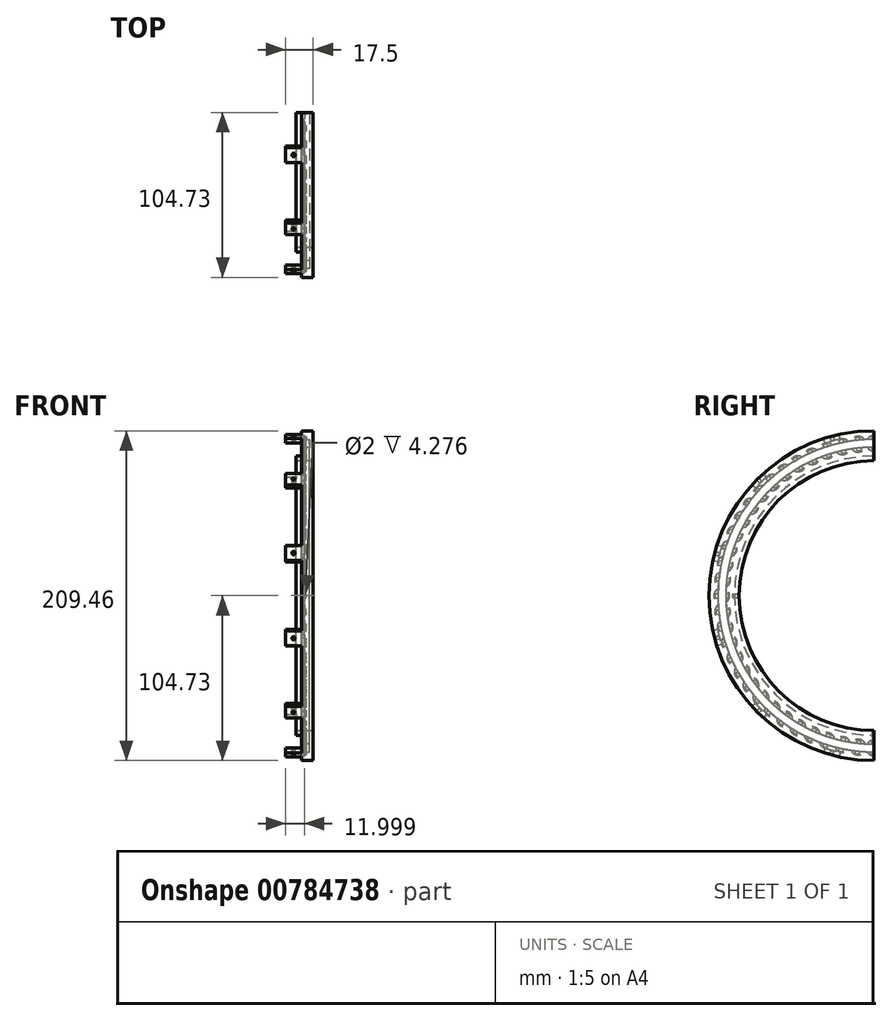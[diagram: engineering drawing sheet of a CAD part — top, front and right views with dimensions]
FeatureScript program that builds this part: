
annotation { "Feature Type Name" : "Feature", "Feature Type Description" : "" }
export const myFeature = defineFeature(function(context is Context, id is Id, definition is map)
    precondition{}
    {
        {
            var Q0;
            Q0=qCreatedBy(makeId("Front.planeOp"),FACE);
            var sketch = newSketch(context, id + "F0", { "sketchPlane" : qUnion([Q0])});
            skLineSegment(sketch, "E0.bottom", {"start": v(-125, 105) * mm, "end": v(125, 105) * mm, "construction": true});
            skLineSegment(sketch, "E0.top", {"start": v(-125, -105) * mm, "end": v(125, -105) * mm, "construction": true});
            skLineSegment(sketch, "E0.left", {"start": v(-125, 105) * mm, "end": v(-125, -105) * mm, "construction": true});
            skLineSegment(sketch, "E0.right", {"start": v(125, 105) * mm, "end": v(125, -105) * mm, "construction": true});
            skLineSegment(sketch, "E1", {"start": v(-16.75, 85.73) * mm, "end": v(-16.75, 88.73) * mm});
            skLineSegment(sketch, "E2", {"start": v(-16.75, 88.73) * mm, "end": v(-13.25, 88.73) * mm});
            skLineSegment(sketch, "E3", {"start": v(-16.75, 85.73) * mm, "end": v(-5.75, 85.73) * mm});
            skLineSegment(sketch, "E4", {"start": v(-5.75, 85.73) * mm, "end": v(-5.75, 104.73) * mm});
            skLineSegment(sketch, "E5", {"start": v(-13.25, 104.73) * mm, "end": v(-13.25, 99.23) * mm});
            skLineSegment(sketch, "E6", {"start": v(-13.25, 99.23) * mm, "end": v(-8.25, 99.23) * mm});
            skLineSegment(sketch, "E7", {"start": v(-8.25, 99.23) * mm, "end": v(-8.25, 94.23) * mm});
            skLineSegment(sketch, "E8", {"start": v(-8.25, 94.23) * mm, "end": v(-13.25, 94.23) * mm});
            skLineSegment(sketch, "E9.trimOffspring", {"start": v(-13.25, 94.23) * mm, "end": v(-13.25, 88.73) * mm});
            skLineSegment(sketch, "E10", {"start": v(-74.95, 0) * mm, "end": v(74.95, 0) * mm});
            skLineSegment(sketch, "E11", {"start": v(-13.25, 104.73) * mm, "end": v(-8.75, 104.73) * mm});
            skLineSegment(sketch, "E12.trimOffspring", {"start": v(-7.75, 104.73) * mm, "end": v(-5.75, 104.73) * mm});
            skLineSegment(sketch, "E13", {"start": v(-7.75, 104.73) * mm, "end": v(-8.75, 104.73) * mm});
            skSolve(sketch);
        }
        {
            var Q0;
            Q0=qSketchRegion(id+"F0",true);
            var Q1;
            Q1=sQuery(id+"F0.wireOp",EDGE,"E10");
            revolve(context, id + "F1", {"surfaceOperationType" : NewSurfaceOperationType.NEW, "entities" : qUnion([Q0]), "axis" : qUnion([Q1]), "revolveType" : RevolveType.ONE_DIRECTION, "angle" : 180 * degree});
        }
        {
            var Q0;
            Q0=qCreatedBy(makeId("Top.planeOp"),FACE);
            cPlane(context, id + "F2", {"entities" : qUnion([Q0]), "cplaneType" : CPlaneType.OFFSET, "offset" : 80 * mm, "oppositeDirection" : true, "width" : 150 * mm, "height" : 150 * mm});
        }
        {
            var Q0;
            Q0=qCreatedBy(id+"F2.planeOp",FACE);
            var sketch = newSketch(context, id + "F3", { "sketchPlane" : qUnion([Q0])});
            skLineSegment(sketch, "E14.top", {"start": v(-9.65, -3.1) * mm, "end": v(-12.85, -3.1) * mm, "construction": true});
            skLineSegment(sketch, "E14.left", {"start": v(-9.65, 0) * mm, "end": v(-9.65, -3.1) * mm, "construction": true});
            skLineSegment(sketch, "E14.right", {"start": v(-12.85, 0) * mm, "end": v(-12.85, -3.1) * mm, "construction": true});
            skLineSegment(sketch, "E15.top", {"start": v(-9.65, 1.57) * mm, "end": v(-12.85, 1.57) * mm, "construction": true});
            skLineSegment(sketch, "E15.left", {"start": v(-9.65, 0) * mm, "end": v(-9.65, 1.57) * mm, "construction": true});
            skLineSegment(sketch, "E15.right", {"start": v(-12.85, 0) * mm, "end": v(-12.85, 1.57) * mm, "construction": true});
            skLineSegment(sketch, "E16", {"start": v(-9.65, 0) * mm, "end": v(-12.85, 0) * mm, "construction": true});
            skLineSegment(sketch, "E17", {"start": v(-11.25, -3.1) * mm, "end": v(-11.25, 0) * mm, "construction": true});
            skCircle(sketch, "E18", {"center": v(-11.25, 0) * mm, "radius": 1 * mm});
            skSolve(sketch);
        }
        {
            var Q0;
            Q0=qSketchRegion(id+"F3",true);
            var Q1;
            Q1=makeQuery(id+"F1.opRevolve","SWEPT_FACE",FACE,{"disambiguationData":[OSD([sQuery(id+"F0.wireOp",EDGE,"E2")])]});
            extrude(context, id + "F4", {"entities" : qUnion([Q0]), "operationType" : NewBodyOperationType.REMOVE, "oppositeDirection" : true, "depth" : 10 * mm, "endBoundEntityFace" : qUnion([Q1]), "offsetDistance" : 25 * mm});
        }
        {
            var Q0;
            Q0=qCreatedBy(makeId("Front.planeOp"),FACE);
            cPlane(context, id + "F5", {"entities" : qUnion([Q0]), "cplaneType" : CPlaneType.OFFSET, "offset" : 80 * mm, "width" : 150 * mm, "height" : 150 * mm});
        }
        {
            var Q0;
            Q0=qCreatedBy(makeId("Top.planeOp"),FACE);
            cPlane(context, id + "F6", {"entities" : qUnion([Q0]), "cplaneType" : CPlaneType.OFFSET, "offset" : 80 * mm, "width" : 150 * mm, "height" : 150 * mm});
        }
        {
            var Q0;
            Q0=qCreatedBy(id+"F5.planeOp",FACE);
            var sketch = newSketch(context, id + "F7", { "sketchPlane" : qUnion([Q0])});
            skLineSegment(sketch, "E19.bottom", {"start": v(-9.65, -3.1) * mm, "end": v(-12.85, -3.1) * mm, "construction": true});
            skLineSegment(sketch, "E19.top", {"start": v(-9.65, 3.1) * mm, "end": v(-12.85, 3.1) * mm, "construction": true});
            skLineSegment(sketch, "E19.left", {"start": v(-9.65, -3.1) * mm, "end": v(-9.65, 3.1) * mm, "construction": true});
            skLineSegment(sketch, "E19.right", {"start": v(-12.85, -3.1) * mm, "end": v(-12.85, 3.1) * mm, "construction": true});
            skLineSegment(sketch, "E20", {"start": v(-11.25, 3.1) * mm, "end": v(-11.25, -3.1) * mm, "construction": true});
            skLineSegment(sketch, "E21", {"start": v(-12.85, 0) * mm, "end": v(-9.65, 0) * mm, "construction": true});
            skCircle(sketch, "E22", {"center": v(-11.25, 0) * mm, "radius": 1 * mm});
            skSolve(sketch);
        }
        {
            var Q0;
            Q0=qSketchRegion(id+"F7",true);
            var Q1;
            Q1=makeQuery(id+"F1.opRevolve","SWEPT_FACE",FACE,{"disambiguationData":[OSD([sQuery(id+"F0.wireOp",EDGE,"E2")])]});
            extrude(context, id + "F8", {"entities" : qUnion([Q0]), "operationType" : NewBodyOperationType.REMOVE, "depth" : 10 * mm, "endBoundEntityFace" : qUnion([Q1]), "offsetDistance" : 25 * mm});
        }
        {
            var Q0;
            Q0=qCreatedBy(id+"F6.planeOp",FACE);
            var sketch = newSketch(context, id + "F9", { "sketchPlane" : qUnion([Q0])});
            skLineSegment(sketch, "E23.bottom", {"start": v(-9.65, 0) * mm, "end": v(-12.85, 0) * mm, "construction": true});
            skLineSegment(sketch, "E23.top", {"start": v(-9.65, -3.1) * mm, "end": v(-12.85, -3.1) * mm, "construction": true});
            skLineSegment(sketch, "E23.left", {"start": v(-9.65, 0) * mm, "end": v(-9.65, -3.1) * mm, "construction": true});
            skLineSegment(sketch, "E23.right", {"start": v(-12.85, 0) * mm, "end": v(-12.85, -3.1) * mm, "construction": true});
            skLineSegment(sketch, "E24", {"start": v(-11.25, 0) * mm, "end": v(-11.25, -3.1) * mm, "construction": true});
            skCircle(sketch, "E25", {"center": v(-11.25, 0) * mm, "radius": 1 * mm});
            skSolve(sketch);
        }
        {
            var Q0;
            Q0=qSketchRegion(id+"F9",true);
            var Q1;
            Q1=makeQuery(id+"F1.opRevolve","SWEPT_FACE",FACE,{"disambiguationData":[OSD([sQuery(id+"F0.wireOp",EDGE,"E2")])]});
            extrude(context, id + "F10", {"entities" : qUnion([Q0]), "operationType" : NewBodyOperationType.REMOVE, "depth" : 10 * mm, "endBoundEntityFace" : qUnion([Q1]), "offsetDistance" : 25 * mm});
        }
        {
            var Q0;
            Q0=makeQuery(id+"F1.opRevolve","SWEPT_FACE",FACE,{"disambiguationData":[OSD([sQuery(id+"F0.wireOp",EDGE,"E7")])]});
            var sketch = newSketch(context, id + "F11", { "sketchPlane" : qUnion([Q0])});
            skCircle(sketch, "E26", {"center": v(0, 96.73) * mm, "radius": 5 * mm});
            skCircle(sketch, "E27.1.0", {"center": v(-10.11, 96.2) * mm, "radius": 5 * mm});
            skCircle(sketch, "E27.2.0", {"center": v(-20.11, 94.62) * mm, "radius": 5 * mm});
            skCircle(sketch, "E27.3.0", {"center": v(-29.9, 92) * mm, "radius": 5 * mm});
            skCircle(sketch, "E27.4.0", {"center": v(-39.34, 88.37) * mm, "radius": 5 * mm});
            skCircle(sketch, "E27.5.0", {"center": v(-48.36, 83.77) * mm, "radius": 5 * mm});
            skCircle(sketch, "E27.6.0", {"center": v(-56.86, 78.26) * mm, "radius": 5 * mm});
            skCircle(sketch, "E27.7.0", {"center": v(-64.73, 71.88) * mm, "radius": 5 * mm});
            skCircle(sketch, "E27.8.0", {"center": v(-71.88, 64.73) * mm, "radius": 5 * mm});
            skCircle(sketch, "E27.9.0", {"center": v(-78.26, 56.86) * mm, "radius": 5 * mm});
            skCircle(sketch, "E27.10.0", {"center": v(-83.77, 48.36) * mm, "radius": 5 * mm});
            skCircle(sketch, "E27.11.0", {"center": v(-88.37, 39.34) * mm, "radius": 5 * mm});
            skCircle(sketch, "E27.12.0", {"center": v(-92, 29.9) * mm, "radius": 5 * mm});
            skCircle(sketch, "E27.13.0", {"center": v(-94.62, 20.11) * mm, "radius": 5 * mm});
            skCircle(sketch, "E27.14.0", {"center": v(-96.2, 10.11) * mm, "radius": 5 * mm});
            skCircle(sketch, "E27.15.0", {"center": v(-96.73, 0) * mm, "radius": 5 * mm});
            skCircle(sketch, "E27.16.0", {"center": v(-96.2, -10.11) * mm, "radius": 5 * mm});
            skCircle(sketch, "E27.17.0", {"center": v(-94.62, -20.11) * mm, "radius": 5 * mm});
            skCircle(sketch, "E27.18.0", {"center": v(-92, -29.9) * mm, "radius": 5 * mm});
            skCircle(sketch, "E27.19.0", {"center": v(-88.37, -39.34) * mm, "radius": 5 * mm});
            skCircle(sketch, "E27.20.0", {"center": v(-83.77, -48.36) * mm, "radius": 5 * mm});
            skCircle(sketch, "E27.21.0", {"center": v(-78.26, -56.86) * mm, "radius": 5 * mm});
            skCircle(sketch, "E27.22.0", {"center": v(-71.88, -64.73) * mm, "radius": 5 * mm});
            skCircle(sketch, "E27.23.0", {"center": v(-64.73, -71.88) * mm, "radius": 5 * mm});
            skCircle(sketch, "E27.24.0", {"center": v(-56.86, -78.26) * mm, "radius": 5 * mm});
            skCircle(sketch, "E27.25.0", {"center": v(-48.36, -83.77) * mm, "radius": 5 * mm});
            skCircle(sketch, "E27.26.0", {"center": v(-39.34, -88.37) * mm, "radius": 5 * mm});
            skCircle(sketch, "E27.27.0", {"center": v(-29.9, -92) * mm, "radius": 5 * mm});
            skCircle(sketch, "E27.28.0", {"center": v(-20.11, -94.62) * mm, "radius": 5 * mm});
            skCircle(sketch, "E27.29.0", {"center": v(-10.11, -96.2) * mm, "radius": 5 * mm});
            skCircle(sketch, "E27.30.0", {"center": v(0, -96.73) * mm, "radius": 5 * mm});
            skCircle(sketch, "E27.31.0", {"center": v(10.11, -96.2) * mm, "radius": 5 * mm});
            skCircle(sketch, "E27.32.0", {"center": v(20.11, -94.62) * mm, "radius": 5 * mm});
            skCircle(sketch, "E27.33.0", {"center": v(29.9, -92) * mm, "radius": 5 * mm});
            skCircle(sketch, "E27.34.0", {"center": v(39.34, -88.37) * mm, "radius": 5 * mm});
            skCircle(sketch, "E27.35.0", {"center": v(48.36, -83.77) * mm, "radius": 5 * mm});
            skCircle(sketch, "E27.36.0", {"center": v(56.86, -78.26) * mm, "radius": 5 * mm});
            skCircle(sketch, "E27.37.0", {"center": v(64.73, -71.88) * mm, "radius": 5 * mm});
            skCircle(sketch, "E27.38.0", {"center": v(71.88, -64.73) * mm, "radius": 5 * mm});
            skCircle(sketch, "E27.39.0", {"center": v(78.26, -56.86) * mm, "radius": 5 * mm});
            skCircle(sketch, "E27.40.0", {"center": v(83.77, -48.37) * mm, "radius": 5 * mm});
            skCircle(sketch, "E27.41.0", {"center": v(88.37, -39.34) * mm, "radius": 5 * mm});
            skCircle(sketch, "E27.42.0", {"center": v(92, -29.9) * mm, "radius": 5 * mm});
            skCircle(sketch, "E27.43.0", {"center": v(94.62, -20.11) * mm, "radius": 5 * mm});
            skCircle(sketch, "E27.44.0", {"center": v(96.2, -10.11) * mm, "radius": 5 * mm});
            skCircle(sketch, "E27.45.0", {"center": v(96.73, 0) * mm, "radius": 5 * mm});
            skCircle(sketch, "E27.46.0", {"center": v(96.2, 10.11) * mm, "radius": 5 * mm});
            skCircle(sketch, "E27.47.0", {"center": v(94.62, 20.11) * mm, "radius": 5 * mm});
            skCircle(sketch, "E27.48.0", {"center": v(92, 29.9) * mm, "radius": 5 * mm});
            skCircle(sketch, "E27.49.0", {"center": v(88.37, 39.34) * mm, "radius": 5 * mm});
            skCircle(sketch, "E27.50.0", {"center": v(83.77, 48.36) * mm, "radius": 5 * mm});
            skCircle(sketch, "E27.51.0", {"center": v(78.26, 56.86) * mm, "radius": 5 * mm});
            skCircle(sketch, "E27.52.0", {"center": v(71.88, 64.73) * mm, "radius": 5 * mm});
            skCircle(sketch, "E27.53.0", {"center": v(64.73, 71.88) * mm, "radius": 5 * mm});
            skCircle(sketch, "E27.54.0", {"center": v(56.86, 78.26) * mm, "radius": 5 * mm});
            skCircle(sketch, "E27.55.0", {"center": v(48.36, 83.77) * mm, "radius": 5 * mm});
            skCircle(sketch, "E27.56.0", {"center": v(39.34, 88.37) * mm, "radius": 5 * mm});
            skCircle(sketch, "E27.57.0", {"center": v(29.9, 92) * mm, "radius": 5 * mm});
            skCircle(sketch, "E27.58.0", {"center": v(20.11, 94.62) * mm, "radius": 5 * mm});
            skCircle(sketch, "E27.59.0", {"center": v(10.11, 96.2) * mm, "radius": 5 * mm});
            skPoint(sketch, "E27.center", {"position": v(0, 0) * mm});
            skSolve(sketch);
        }
        {
            var Q0;
            Q0=qSketchRegion(id+"F11",true);
            extrude(context, id + "F12", {"entities" : qUnion([Q0]), "operationType" : NewBodyOperationType.REMOVE, "depth" : 25 * mm, "offsetDistance" : 25 * mm, "hasSecondDirection" : true, "secondDirectionOppositeDirection" : false, "secondDirectionDepth" : 3 * mm});
        }
        {
            var Q0;
            Q0=makeQuery(id+"F1.opRevolve","SWEPT_FACE",FACE,{"disambiguationData":[OSD([sQuery(id+"F0.wireOp",EDGE,"E7")])]});
            var sketch = newSketch(context, id + "F13", { "sketchPlane" : qUnion([Q0])});
            skLineSegment(sketch, "E28.bottom", {"start": v(1.36, 92.48) * mm, "end": v(0, 92.48) * mm});
            skLineSegment(sketch, "E28.top", {"start": v(1.36, 100.98) * mm, "end": v(0, 100.98) * mm});
            skLineSegment(sketch, "E28.left", {"start": v(1.36, 92.48) * mm, "end": v(1.36, 100.98) * mm});
            skLineSegment(sketch, "E29", {"start": v(1.96, 96.73) * mm, "end": v(-1.46, 96.73) * mm, "construction": true});
            skLineSegment(sketch, "E30.MirrorCS", {"start": v(-1.36, 92.48) * mm, "end": v(0, 92.48) * mm});
            skLineSegment(sketch, "E31.MirrorCS", {"start": v(-1.36, 92.48) * mm, "end": v(-1.36, 100.98) * mm});
            skLineSegment(sketch, "E32.MirrorCS", {"start": v(-1.36, 100.98) * mm, "end": v(0, 100.98) * mm});
            skLineSegment(sketch, "E33", {"start": v(0, 92.48) * mm, "end": v(0, 100.98) * mm, "construction": true});
            skLineSegment(sketch, "E34.1.0", {"start": v(-8.32, 92.12) * mm, "end": v(-9.67, 91.97) * mm});
            skLineSegment(sketch, "E34.1.1", {"start": v(-9.2, 100.57) * mm, "end": v(-10.56, 100.43) * mm});
            skLineSegment(sketch, "E34.1.2", {"start": v(-8.32, 92.12) * mm, "end": v(-9.2, 100.57) * mm});
            skLineSegment(sketch, "E34.1.3", {"start": v(-8.16, 96.4) * mm, "end": v(-11.56, 96.05) * mm, "construction": true});
            skLineSegment(sketch, "E34.1.4", {"start": v(-11.02, 91.83) * mm, "end": v(-9.67, 91.97) * mm});
            skLineSegment(sketch, "E34.1.5", {"start": v(-11.02, 91.83) * mm, "end": v(-11.9, 100.28) * mm});
            skLineSegment(sketch, "E34.1.6", {"start": v(-11.9, 100.28) * mm, "end": v(-10.56, 100.43) * mm});
            skLineSegment(sketch, "E34.1.7", {"start": v(-9.67, 91.97) * mm, "end": v(-10.56, 100.43) * mm, "construction": true});
            skLineSegment(sketch, "E34.2.0", {"start": v(-17.9, 90.74) * mm, "end": v(-19.23, 90.46) * mm});
            skLineSegment(sketch, "E34.2.1", {"start": v(-19.67, 99.06) * mm, "end": v(-21, 98.77) * mm});
            skLineSegment(sketch, "E34.2.2", {"start": v(-17.9, 90.74) * mm, "end": v(-19.67, 99.06) * mm});
            skLineSegment(sketch, "E34.2.3", {"start": v(-18.2, 95.02) * mm, "end": v(-21.54, 94.31) * mm, "construction": true});
            skLineSegment(sketch, "E34.2.4", {"start": v(-20.56, 90.18) * mm, "end": v(-19.23, 90.46) * mm});
            skLineSegment(sketch, "E34.2.5", {"start": v(-20.56, 90.18) * mm, "end": v(-22.32, 98.5) * mm});
            skLineSegment(sketch, "E34.2.6", {"start": v(-22.32, 98.5) * mm, "end": v(-21, 98.77) * mm});
            skLineSegment(sketch, "E34.2.7", {"start": v(-19.23, 90.46) * mm, "end": v(-21, 98.77) * mm, "construction": true});
            skLineSegment(sketch, "E34.3.0", {"start": v(-27.29, 88.37) * mm, "end": v(-28.58, 87.95) * mm});
            skLineSegment(sketch, "E34.3.1", {"start": v(-29.91, 96.46) * mm, "end": v(-31.2, 96.04) * mm});
            skLineSegment(sketch, "E34.3.2", {"start": v(-27.29, 88.37) * mm, "end": v(-29.91, 96.46) * mm});
            skLineSegment(sketch, "E34.3.3", {"start": v(-28.02, 92.6) * mm, "end": v(-31.28, 91.54) * mm, "construction": true});
            skLineSegment(sketch, "E34.3.4", {"start": v(-29.87, 87.53) * mm, "end": v(-28.58, 87.95) * mm});
            skLineSegment(sketch, "E34.3.5", {"start": v(-29.87, 87.53) * mm, "end": v(-32.5, 95.62) * mm});
            skLineSegment(sketch, "E34.3.6", {"start": v(-32.5, 95.62) * mm, "end": v(-31.2, 96.04) * mm});
            skLineSegment(sketch, "E34.3.7", {"start": v(-28.58, 87.95) * mm, "end": v(-31.2, 96.04) * mm, "construction": true});
            skLineSegment(sketch, "E34.4.0", {"start": v(-36.37, 85.04) * mm, "end": v(-37.62, 84.48) * mm});
            skLineSegment(sketch, "E34.4.1", {"start": v(-39.83, 92.8) * mm, "end": v(-41.07, 92.25) * mm});
            skLineSegment(sketch, "E34.4.2", {"start": v(-36.37, 85.04) * mm, "end": v(-39.83, 92.8) * mm});
            skLineSegment(sketch, "E34.4.3", {"start": v(-37.55, 89.17) * mm, "end": v(-40.68, 87.77) * mm, "construction": true});
            skLineSegment(sketch, "E34.4.4", {"start": v(-38.86, 83.93) * mm, "end": v(-37.62, 84.48) * mm});
            skLineSegment(sketch, "E34.4.5", {"start": v(-38.86, 83.93) * mm, "end": v(-42.31, 91.7) * mm});
            skLineSegment(sketch, "E34.4.6", {"start": v(-42.31, 91.7) * mm, "end": v(-41.07, 92.25) * mm});
            skLineSegment(sketch, "E34.4.7", {"start": v(-37.62, 84.48) * mm, "end": v(-41.07, 92.25) * mm, "construction": true});
            skLineSegment(sketch, "E34.5.0", {"start": v(-45.06, 80.77) * mm, "end": v(-46.24, 80.1) * mm});
            skLineSegment(sketch, "E34.5.1", {"start": v(-49.31, 88.13) * mm, "end": v(-50.49, 87.45) * mm});
            skLineSegment(sketch, "E34.5.2", {"start": v(-45.06, 80.77) * mm, "end": v(-49.31, 88.13) * mm});
            skLineSegment(sketch, "E34.5.3", {"start": v(-46.67, 84.75) * mm, "end": v(-49.63, 83.04) * mm, "construction": true});
            skLineSegment(sketch, "E34.5.4", {"start": v(-47.42, 79.41) * mm, "end": v(-46.24, 80.1) * mm});
            skLineSegment(sketch, "E34.5.5", {"start": v(-47.42, 79.41) * mm, "end": v(-51.67, 86.77) * mm});
            skLineSegment(sketch, "E34.5.6", {"start": v(-51.67, 86.77) * mm, "end": v(-50.49, 87.45) * mm});
            skLineSegment(sketch, "E34.5.7", {"start": v(-46.24, 80.1) * mm, "end": v(-50.49, 87.45) * mm, "construction": true});
            skLineSegment(sketch, "E34.6.0", {"start": v(-53.26, 75.62) * mm, "end": v(-54.36, 74.82) * mm});
            skLineSegment(sketch, "E34.6.1", {"start": v(-58.26, 82.5) * mm, "end": v(-59.35, 81.7) * mm});
            skLineSegment(sketch, "E34.6.2", {"start": v(-53.26, 75.62) * mm, "end": v(-58.26, 82.5) * mm});
            skLineSegment(sketch, "E34.6.3", {"start": v(-55.27, 79.4) * mm, "end": v(-58.04, 77.4) * mm, "construction": true});
            skLineSegment(sketch, "E34.6.4", {"start": v(-55.46, 74.02) * mm, "end": v(-54.36, 74.82) * mm});
            skLineSegment(sketch, "E34.6.5", {"start": v(-55.46, 74.02) * mm, "end": v(-60.45, 80.9) * mm});
            skLineSegment(sketch, "E34.6.6", {"start": v(-60.45, 80.9) * mm, "end": v(-59.35, 81.7) * mm});
            skLineSegment(sketch, "E34.6.7", {"start": v(-54.36, 74.82) * mm, "end": v(-59.35, 81.7) * mm, "construction": true});
            skLineSegment(sketch, "E34.7.0", {"start": v(-60.87, 69.63) * mm, "end": v(-61.88, 68.73) * mm});
            skLineSegment(sketch, "E34.7.1", {"start": v(-66.56, 75.95) * mm, "end": v(-67.57, 75.04) * mm});
            skLineSegment(sketch, "E34.7.2", {"start": v(-60.87, 69.63) * mm, "end": v(-66.56, 75.95) * mm});
            skLineSegment(sketch, "E34.7.3", {"start": v(-63.27, 73.2) * mm, "end": v(-65.8, 70.9) * mm, "construction": true});
            skLineSegment(sketch, "E34.7.4", {"start": v(-62.9, 67.82) * mm, "end": v(-61.88, 68.73) * mm});
            skLineSegment(sketch, "E34.7.5", {"start": v(-62.9, 67.82) * mm, "end": v(-68.58, 74.13) * mm});
            skLineSegment(sketch, "E34.7.6", {"start": v(-68.58, 74.13) * mm, "end": v(-67.57, 75.04) * mm});
            skLineSegment(sketch, "E34.7.7", {"start": v(-61.88, 68.73) * mm, "end": v(-67.57, 75.04) * mm, "construction": true});
            skLineSegment(sketch, "E34.8.0", {"start": v(-67.82, 62.9) * mm, "end": v(-68.73, 61.88) * mm});
            skLineSegment(sketch, "E34.8.1", {"start": v(-74.13, 68.58) * mm, "end": v(-75.04, 67.57) * mm});
            skLineSegment(sketch, "E34.8.2", {"start": v(-67.82, 62.9) * mm, "end": v(-74.13, 68.58) * mm});
            skLineSegment(sketch, "E34.8.3", {"start": v(-70.57, 66.18) * mm, "end": v(-72.86, 63.64) * mm, "construction": true});
            skLineSegment(sketch, "E34.8.4", {"start": v(-69.63, 60.87) * mm, "end": v(-68.73, 61.88) * mm});
            skLineSegment(sketch, "E34.8.5", {"start": v(-69.63, 60.87) * mm, "end": v(-75.95, 66.56) * mm});
            skLineSegment(sketch, "E34.8.6", {"start": v(-75.95, 66.56) * mm, "end": v(-75.04, 67.57) * mm});
            skLineSegment(sketch, "E34.8.7", {"start": v(-68.73, 61.88) * mm, "end": v(-75.04, 67.57) * mm, "construction": true});
            skLineSegment(sketch, "E34.9.0", {"start": v(-74.02, 55.46) * mm, "end": v(-74.82, 54.36) * mm});
            skLineSegment(sketch, "E34.9.1", {"start": v(-80.9, 60.45) * mm, "end": v(-81.7, 59.35) * mm});
            skLineSegment(sketch, "E34.9.2", {"start": v(-74.02, 55.46) * mm, "end": v(-80.9, 60.45) * mm});
            skLineSegment(sketch, "E34.9.3", {"start": v(-77.1, 58.44) * mm, "end": v(-79.11, 55.68) * mm, "construction": true});
            skLineSegment(sketch, "E34.9.4", {"start": v(-75.62, 53.26) * mm, "end": v(-74.82, 54.36) * mm});
            skLineSegment(sketch, "E34.9.5", {"start": v(-75.62, 53.26) * mm, "end": v(-82.5, 58.26) * mm});
            skLineSegment(sketch, "E34.9.6", {"start": v(-82.5, 58.26) * mm, "end": v(-81.7, 59.35) * mm});
            skLineSegment(sketch, "E34.9.7", {"start": v(-74.82, 54.36) * mm, "end": v(-81.7, 59.35) * mm, "construction": true});
            skLineSegment(sketch, "E34.10.0", {"start": v(-79.41, 47.42) * mm, "end": v(-80.1, 46.24) * mm});
            skLineSegment(sketch, "E34.10.1", {"start": v(-86.77, 51.67) * mm, "end": v(-87.45, 50.49) * mm});
            skLineSegment(sketch, "E34.10.2", {"start": v(-79.41, 47.42) * mm, "end": v(-86.77, 51.67) * mm});
            skLineSegment(sketch, "E34.10.3", {"start": v(-82.79, 50.06) * mm, "end": v(-84.5, 47.1) * mm, "construction": true});
            skLineSegment(sketch, "E34.10.4", {"start": v(-80.77, 45.06) * mm, "end": v(-80.1, 46.24) * mm});
            skLineSegment(sketch, "E34.10.5", {"start": v(-80.77, 45.06) * mm, "end": v(-88.13, 49.31) * mm});
            skLineSegment(sketch, "E34.10.6", {"start": v(-88.13, 49.31) * mm, "end": v(-87.45, 50.49) * mm});
            skLineSegment(sketch, "E34.10.7", {"start": v(-80.1, 46.24) * mm, "end": v(-87.45, 50.49) * mm, "construction": true});
            skLineSegment(sketch, "E34.11.0", {"start": v(-83.93, 38.86) * mm, "end": v(-84.48, 37.62) * mm});
            skLineSegment(sketch, "E34.11.1", {"start": v(-91.7, 42.31) * mm, "end": v(-92.25, 41.07) * mm});
            skLineSegment(sketch, "E34.11.2", {"start": v(-83.93, 38.86) * mm, "end": v(-91.7, 42.31) * mm});
            skLineSegment(sketch, "E34.11.3", {"start": v(-87.57, 41.14) * mm, "end": v(-88.96, 38) * mm, "construction": true});
            skLineSegment(sketch, "E34.11.4", {"start": v(-85.04, 36.37) * mm, "end": v(-84.48, 37.62) * mm});
            skLineSegment(sketch, "E34.11.5", {"start": v(-85.04, 36.37) * mm, "end": v(-92.8, 39.83) * mm});
            skLineSegment(sketch, "E34.11.6", {"start": v(-92.8, 39.83) * mm, "end": v(-92.25, 41.07) * mm});
            skLineSegment(sketch, "E34.11.7", {"start": v(-84.48, 37.62) * mm, "end": v(-92.25, 41.07) * mm, "construction": true});
            skLineSegment(sketch, "E34.12.0", {"start": v(-87.53, 29.87) * mm, "end": v(-87.95, 28.58) * mm});
            skLineSegment(sketch, "E34.12.1", {"start": v(-95.62, 32.5) * mm, "end": v(-96.04, 31.2) * mm});
            skLineSegment(sketch, "E34.12.2", {"start": v(-87.53, 29.87) * mm, "end": v(-95.62, 32.5) * mm});
            skLineSegment(sketch, "E34.12.3", {"start": v(-91.39, 31.76) * mm, "end": v(-92.45, 28.5) * mm, "construction": true});
            skLineSegment(sketch, "E34.12.4", {"start": v(-88.37, 27.29) * mm, "end": v(-87.95, 28.58) * mm});
            skLineSegment(sketch, "E34.12.5", {"start": v(-88.37, 27.29) * mm, "end": v(-96.46, 29.91) * mm});
            skLineSegment(sketch, "E34.12.6", {"start": v(-96.46, 29.91) * mm, "end": v(-96.04, 31.2) * mm});
            skLineSegment(sketch, "E34.12.7", {"start": v(-87.95, 28.58) * mm, "end": v(-96.04, 31.2) * mm, "construction": true});
            skLineSegment(sketch, "E34.13.0", {"start": v(-90.18, 20.56) * mm, "end": v(-90.46, 19.23) * mm});
            skLineSegment(sketch, "E34.13.1", {"start": v(-98.5, 22.32) * mm, "end": v(-98.77, 21) * mm});
            skLineSegment(sketch, "E34.13.2", {"start": v(-90.18, 20.56) * mm, "end": v(-98.5, 22.32) * mm});
            skLineSegment(sketch, "E34.13.3", {"start": v(-94.2, 22.03) * mm, "end": v(-94.92, 18.68) * mm, "construction": true});
            skLineSegment(sketch, "E34.13.4", {"start": v(-90.74, 17.9) * mm, "end": v(-90.46, 19.23) * mm});
            skLineSegment(sketch, "E34.13.5", {"start": v(-90.74, 17.9) * mm, "end": v(-99.06, 19.67) * mm});
            skLineSegment(sketch, "E34.13.6", {"start": v(-99.06, 19.67) * mm, "end": v(-98.77, 21) * mm});
            skLineSegment(sketch, "E34.13.7", {"start": v(-90.46, 19.23) * mm, "end": v(-98.77, 21) * mm, "construction": true});
            skLineSegment(sketch, "E34.14.0", {"start": v(-91.83, 11.02) * mm, "end": v(-91.97, 9.67) * mm});
            skLineSegment(sketch, "E34.14.1", {"start": v(-100.28, 11.9) * mm, "end": v(-100.43, 10.56) * mm});
            skLineSegment(sketch, "E34.14.2", {"start": v(-91.83, 11.02) * mm, "end": v(-100.28, 11.9) * mm});
            skLineSegment(sketch, "E34.14.3", {"start": v(-96, 12.06) * mm, "end": v(-96.35, 8.66) * mm, "construction": true});
            skLineSegment(sketch, "E34.14.4", {"start": v(-92.12, 8.32) * mm, "end": v(-91.97, 9.67) * mm});
            skLineSegment(sketch, "E34.14.5", {"start": v(-92.12, 8.32) * mm, "end": v(-100.57, 9.2) * mm});
            skLineSegment(sketch, "E34.14.6", {"start": v(-100.57, 9.2) * mm, "end": v(-100.43, 10.56) * mm});
            skLineSegment(sketch, "E34.14.7", {"start": v(-91.97, 9.67) * mm, "end": v(-100.43, 10.56) * mm, "construction": true});
            skLineSegment(sketch, "E34.15.0", {"start": v(-92.48, 1.36) * mm, "end": v(-92.48, 0) * mm});
            skLineSegment(sketch, "E34.15.1", {"start": v(-100.98, 1.36) * mm, "end": v(-100.98, 0) * mm});
            skLineSegment(sketch, "E34.15.2", {"start": v(-92.48, 1.36) * mm, "end": v(-100.98, 1.36) * mm});
            skLineSegment(sketch, "E34.15.3", {"start": v(-96.73, 1.96) * mm, "end": v(-96.73, -1.46) * mm, "construction": true});
            skLineSegment(sketch, "E34.15.4", {"start": v(-92.48, -1.36) * mm, "end": v(-92.48, 0) * mm});
            skLineSegment(sketch, "E34.15.5", {"start": v(-92.48, -1.36) * mm, "end": v(-100.98, -1.36) * mm});
            skLineSegment(sketch, "E34.15.6", {"start": v(-100.98, -1.36) * mm, "end": v(-100.98, 0) * mm});
            skLineSegment(sketch, "E34.15.7", {"start": v(-92.48, 0) * mm, "end": v(-100.98, 0) * mm, "construction": true});
            skLineSegment(sketch, "E34.16.0", {"start": v(-92.12, -8.32) * mm, "end": v(-91.97, -9.67) * mm});
            skLineSegment(sketch, "E34.16.1", {"start": v(-100.57, -9.2) * mm, "end": v(-100.43, -10.56) * mm});
            skLineSegment(sketch, "E34.16.2", {"start": v(-92.12, -8.32) * mm, "end": v(-100.57, -9.2) * mm});
            skLineSegment(sketch, "E34.16.3", {"start": v(-96.4, -8.16) * mm, "end": v(-96.05, -11.56) * mm, "construction": true});
            skLineSegment(sketch, "E34.16.4", {"start": v(-91.83, -11.02) * mm, "end": v(-91.97, -9.67) * mm});
            skLineSegment(sketch, "E34.16.5", {"start": v(-91.83, -11.02) * mm, "end": v(-100.28, -11.9) * mm});
            skLineSegment(sketch, "E34.16.6", {"start": v(-100.28, -11.9) * mm, "end": v(-100.43, -10.56) * mm});
            skLineSegment(sketch, "E34.16.7", {"start": v(-91.97, -9.67) * mm, "end": v(-100.43, -10.56) * mm, "construction": true});
            skLineSegment(sketch, "E34.17.0", {"start": v(-90.74, -17.9) * mm, "end": v(-90.46, -19.23) * mm});
            skLineSegment(sketch, "E34.17.1", {"start": v(-99.06, -19.67) * mm, "end": v(-98.77, -21) * mm});
            skLineSegment(sketch, "E34.17.2", {"start": v(-90.74, -17.9) * mm, "end": v(-99.06, -19.67) * mm});
            skLineSegment(sketch, "E34.17.3", {"start": v(-95.02, -18.2) * mm, "end": v(-94.31, -21.54) * mm, "construction": true});
            skLineSegment(sketch, "E34.17.4", {"start": v(-90.18, -20.56) * mm, "end": v(-90.46, -19.23) * mm});
            skLineSegment(sketch, "E34.17.5", {"start": v(-90.18, -20.56) * mm, "end": v(-98.5, -22.32) * mm});
            skLineSegment(sketch, "E34.17.6", {"start": v(-98.5, -22.32) * mm, "end": v(-98.77, -21) * mm});
            skLineSegment(sketch, "E34.17.7", {"start": v(-90.46, -19.23) * mm, "end": v(-98.77, -21) * mm, "construction": true});
            skLineSegment(sketch, "E34.18.0", {"start": v(-88.37, -27.29) * mm, "end": v(-87.95, -28.58) * mm});
            skLineSegment(sketch, "E34.18.1", {"start": v(-96.46, -29.91) * mm, "end": v(-96.04, -31.2) * mm});
            skLineSegment(sketch, "E34.18.2", {"start": v(-88.37, -27.29) * mm, "end": v(-96.46, -29.91) * mm});
            skLineSegment(sketch, "E34.18.3", {"start": v(-92.6, -28.02) * mm, "end": v(-91.54, -31.28) * mm, "construction": true});
            skLineSegment(sketch, "E34.18.4", {"start": v(-87.53, -29.87) * mm, "end": v(-87.95, -28.58) * mm});
            skLineSegment(sketch, "E34.18.5", {"start": v(-87.53, -29.87) * mm, "end": v(-95.62, -32.5) * mm});
            skLineSegment(sketch, "E34.18.6", {"start": v(-95.62, -32.5) * mm, "end": v(-96.04, -31.2) * mm});
            skLineSegment(sketch, "E34.18.7", {"start": v(-87.95, -28.58) * mm, "end": v(-96.04, -31.2) * mm, "construction": true});
            skLineSegment(sketch, "E34.19.0", {"start": v(-85.04, -36.37) * mm, "end": v(-84.48, -37.62) * mm});
            skLineSegment(sketch, "E34.19.1", {"start": v(-92.8, -39.83) * mm, "end": v(-92.25, -41.07) * mm});
            skLineSegment(sketch, "E34.19.2", {"start": v(-85.04, -36.37) * mm, "end": v(-92.8, -39.83) * mm});
            skLineSegment(sketch, "E34.19.3", {"start": v(-89.17, -37.55) * mm, "end": v(-87.77, -40.68) * mm, "construction": true});
            skLineSegment(sketch, "E34.19.4", {"start": v(-83.93, -38.86) * mm, "end": v(-84.48, -37.62) * mm});
            skLineSegment(sketch, "E34.19.5", {"start": v(-83.93, -38.86) * mm, "end": v(-91.7, -42.31) * mm});
            skLineSegment(sketch, "E34.19.6", {"start": v(-91.7, -42.31) * mm, "end": v(-92.25, -41.07) * mm});
            skLineSegment(sketch, "E34.19.7", {"start": v(-84.48, -37.62) * mm, "end": v(-92.25, -41.07) * mm, "construction": true});
            skLineSegment(sketch, "E34.20.0", {"start": v(-80.77, -45.06) * mm, "end": v(-80.1, -46.24) * mm});
            skLineSegment(sketch, "E34.20.1", {"start": v(-88.13, -49.31) * mm, "end": v(-87.45, -50.49) * mm});
            skLineSegment(sketch, "E34.20.2", {"start": v(-80.77, -45.06) * mm, "end": v(-88.13, -49.31) * mm});
            skLineSegment(sketch, "E34.20.3", {"start": v(-84.75, -46.67) * mm, "end": v(-83.04, -49.63) * mm, "construction": true});
            skLineSegment(sketch, "E34.20.4", {"start": v(-79.41, -47.42) * mm, "end": v(-80.1, -46.24) * mm});
            skLineSegment(sketch, "E34.20.5", {"start": v(-79.41, -47.42) * mm, "end": v(-86.77, -51.67) * mm});
            skLineSegment(sketch, "E34.20.6", {"start": v(-86.77, -51.67) * mm, "end": v(-87.45, -50.49) * mm});
            skLineSegment(sketch, "E34.20.7", {"start": v(-80.1, -46.24) * mm, "end": v(-87.45, -50.49) * mm, "construction": true});
            skLineSegment(sketch, "E34.21.0", {"start": v(-75.62, -53.26) * mm, "end": v(-74.82, -54.36) * mm});
            skLineSegment(sketch, "E34.21.1", {"start": v(-82.5, -58.26) * mm, "end": v(-81.7, -59.35) * mm});
            skLineSegment(sketch, "E34.21.2", {"start": v(-75.62, -53.26) * mm, "end": v(-82.5, -58.26) * mm});
            skLineSegment(sketch, "E34.21.3", {"start": v(-79.4, -55.27) * mm, "end": v(-77.4, -58.04) * mm, "construction": true});
            skLineSegment(sketch, "E34.21.4", {"start": v(-74.02, -55.46) * mm, "end": v(-74.82, -54.36) * mm});
            skLineSegment(sketch, "E34.21.5", {"start": v(-74.02, -55.46) * mm, "end": v(-80.9, -60.45) * mm});
            skLineSegment(sketch, "E34.21.6", {"start": v(-80.9, -60.45) * mm, "end": v(-81.7, -59.35) * mm});
            skLineSegment(sketch, "E34.21.7", {"start": v(-74.82, -54.36) * mm, "end": v(-81.7, -59.35) * mm, "construction": true});
            skLineSegment(sketch, "E34.22.0", {"start": v(-69.63, -60.87) * mm, "end": v(-68.73, -61.88) * mm});
            skLineSegment(sketch, "E34.22.1", {"start": v(-75.95, -66.56) * mm, "end": v(-75.04, -67.57) * mm});
            skLineSegment(sketch, "E34.22.2", {"start": v(-69.63, -60.87) * mm, "end": v(-75.95, -66.56) * mm});
            skLineSegment(sketch, "E34.22.3", {"start": v(-73.2, -63.27) * mm, "end": v(-70.9, -65.8) * mm, "construction": true});
            skLineSegment(sketch, "E34.22.4", {"start": v(-67.82, -62.9) * mm, "end": v(-68.73, -61.88) * mm});
            skLineSegment(sketch, "E34.22.5", {"start": v(-67.82, -62.9) * mm, "end": v(-74.13, -68.58) * mm});
            skLineSegment(sketch, "E34.22.6", {"start": v(-74.13, -68.58) * mm, "end": v(-75.04, -67.57) * mm});
            skLineSegment(sketch, "E34.22.7", {"start": v(-68.73, -61.88) * mm, "end": v(-75.04, -67.57) * mm, "construction": true});
            skLineSegment(sketch, "E34.23.0", {"start": v(-62.9, -67.82) * mm, "end": v(-61.88, -68.73) * mm});
            skLineSegment(sketch, "E34.23.1", {"start": v(-68.58, -74.13) * mm, "end": v(-67.57, -75.04) * mm});
            skLineSegment(sketch, "E34.23.2", {"start": v(-62.9, -67.82) * mm, "end": v(-68.58, -74.13) * mm});
            skLineSegment(sketch, "E34.23.3", {"start": v(-66.18, -70.57) * mm, "end": v(-63.64, -72.86) * mm, "construction": true});
            skLineSegment(sketch, "E34.23.4", {"start": v(-60.87, -69.63) * mm, "end": v(-61.88, -68.73) * mm});
            skLineSegment(sketch, "E34.23.5", {"start": v(-60.87, -69.63) * mm, "end": v(-66.56, -75.95) * mm});
            skLineSegment(sketch, "E34.23.6", {"start": v(-66.56, -75.95) * mm, "end": v(-67.57, -75.04) * mm});
            skLineSegment(sketch, "E34.23.7", {"start": v(-61.88, -68.73) * mm, "end": v(-67.57, -75.04) * mm, "construction": true});
            skLineSegment(sketch, "E34.24.0", {"start": v(-55.46, -74.02) * mm, "end": v(-54.36, -74.82) * mm});
            skLineSegment(sketch, "E34.24.1", {"start": v(-60.45, -80.9) * mm, "end": v(-59.35, -81.7) * mm});
            skLineSegment(sketch, "E34.24.2", {"start": v(-55.46, -74.02) * mm, "end": v(-60.45, -80.9) * mm});
            skLineSegment(sketch, "E34.24.3", {"start": v(-58.44, -77.1) * mm, "end": v(-55.68, -79.11) * mm, "construction": true});
            skLineSegment(sketch, "E34.24.4", {"start": v(-53.26, -75.62) * mm, "end": v(-54.36, -74.82) * mm});
            skLineSegment(sketch, "E34.24.5", {"start": v(-53.26, -75.62) * mm, "end": v(-58.26, -82.5) * mm});
            skLineSegment(sketch, "E34.24.6", {"start": v(-58.26, -82.5) * mm, "end": v(-59.35, -81.7) * mm});
            skLineSegment(sketch, "E34.24.7", {"start": v(-54.36, -74.82) * mm, "end": v(-59.35, -81.7) * mm, "construction": true});
            skLineSegment(sketch, "E34.25.0", {"start": v(-47.42, -79.41) * mm, "end": v(-46.24, -80.1) * mm});
            skLineSegment(sketch, "E34.25.1", {"start": v(-51.67, -86.77) * mm, "end": v(-50.49, -87.45) * mm});
            skLineSegment(sketch, "E34.25.2", {"start": v(-47.42, -79.41) * mm, "end": v(-51.67, -86.77) * mm});
            skLineSegment(sketch, "E34.25.3", {"start": v(-50.06, -82.79) * mm, "end": v(-47.1, -84.5) * mm, "construction": true});
            skLineSegment(sketch, "E34.25.4", {"start": v(-45.06, -80.77) * mm, "end": v(-46.24, -80.1) * mm});
            skLineSegment(sketch, "E34.25.5", {"start": v(-45.06, -80.77) * mm, "end": v(-49.31, -88.13) * mm});
            skLineSegment(sketch, "E34.25.6", {"start": v(-49.31, -88.13) * mm, "end": v(-50.49, -87.45) * mm});
            skLineSegment(sketch, "E34.25.7", {"start": v(-46.24, -80.1) * mm, "end": v(-50.49, -87.45) * mm, "construction": true});
            skLineSegment(sketch, "E34.26.0", {"start": v(-38.86, -83.93) * mm, "end": v(-37.62, -84.48) * mm});
            skLineSegment(sketch, "E34.26.1", {"start": v(-42.31, -91.7) * mm, "end": v(-41.07, -92.25) * mm});
            skLineSegment(sketch, "E34.26.2", {"start": v(-38.86, -83.93) * mm, "end": v(-42.31, -91.7) * mm});
            skLineSegment(sketch, "E34.26.3", {"start": v(-41.14, -87.57) * mm, "end": v(-38, -88.96) * mm, "construction": true});
            skLineSegment(sketch, "E34.26.4", {"start": v(-36.37, -85.04) * mm, "end": v(-37.62, -84.48) * mm});
            skLineSegment(sketch, "E34.26.5", {"start": v(-36.37, -85.04) * mm, "end": v(-39.83, -92.8) * mm});
            skLineSegment(sketch, "E34.26.6", {"start": v(-39.83, -92.8) * mm, "end": v(-41.07, -92.25) * mm});
            skLineSegment(sketch, "E34.26.7", {"start": v(-37.62, -84.48) * mm, "end": v(-41.07, -92.25) * mm, "construction": true});
            skLineSegment(sketch, "E34.27.0", {"start": v(-29.87, -87.53) * mm, "end": v(-28.58, -87.95) * mm});
            skLineSegment(sketch, "E34.27.1", {"start": v(-32.5, -95.62) * mm, "end": v(-31.2, -96.04) * mm});
            skLineSegment(sketch, "E34.27.2", {"start": v(-29.87, -87.53) * mm, "end": v(-32.5, -95.62) * mm});
            skLineSegment(sketch, "E34.27.3", {"start": v(-31.76, -91.39) * mm, "end": v(-28.5, -92.45) * mm, "construction": true});
            skLineSegment(sketch, "E34.27.4", {"start": v(-27.29, -88.37) * mm, "end": v(-28.58, -87.95) * mm});
            skLineSegment(sketch, "E34.27.5", {"start": v(-27.29, -88.37) * mm, "end": v(-29.91, -96.46) * mm});
            skLineSegment(sketch, "E34.27.6", {"start": v(-29.91, -96.46) * mm, "end": v(-31.2, -96.04) * mm});
            skLineSegment(sketch, "E34.27.7", {"start": v(-28.58, -87.95) * mm, "end": v(-31.2, -96.04) * mm, "construction": true});
            skLineSegment(sketch, "E34.28.0", {"start": v(-20.56, -90.18) * mm, "end": v(-19.23, -90.46) * mm});
            skLineSegment(sketch, "E34.28.1", {"start": v(-22.32, -98.5) * mm, "end": v(-21, -98.77) * mm});
            skLineSegment(sketch, "E34.28.2", {"start": v(-20.56, -90.18) * mm, "end": v(-22.32, -98.5) * mm});
            skLineSegment(sketch, "E34.28.3", {"start": v(-22.03, -94.2) * mm, "end": v(-18.68, -94.92) * mm, "construction": true});
            skLineSegment(sketch, "E34.28.4", {"start": v(-17.9, -90.74) * mm, "end": v(-19.23, -90.46) * mm});
            skLineSegment(sketch, "E34.28.5", {"start": v(-17.9, -90.74) * mm, "end": v(-19.67, -99.06) * mm});
            skLineSegment(sketch, "E34.28.6", {"start": v(-19.67, -99.06) * mm, "end": v(-21, -98.77) * mm});
            skLineSegment(sketch, "E34.28.7", {"start": v(-19.23, -90.46) * mm, "end": v(-21, -98.77) * mm, "construction": true});
            skLineSegment(sketch, "E34.29.0", {"start": v(-11.02, -91.83) * mm, "end": v(-9.67, -91.97) * mm});
            skLineSegment(sketch, "E34.29.1", {"start": v(-11.9, -100.28) * mm, "end": v(-10.56, -100.43) * mm});
            skLineSegment(sketch, "E34.29.2", {"start": v(-11.02, -91.83) * mm, "end": v(-11.9, -100.28) * mm});
            skLineSegment(sketch, "E34.29.3", {"start": v(-12.06, -96) * mm, "end": v(-8.66, -96.35) * mm, "construction": true});
            skLineSegment(sketch, "E34.29.4", {"start": v(-8.32, -92.12) * mm, "end": v(-9.67, -91.97) * mm});
            skLineSegment(sketch, "E34.29.5", {"start": v(-8.32, -92.12) * mm, "end": v(-9.2, -100.57) * mm});
            skLineSegment(sketch, "E34.29.6", {"start": v(-9.2, -100.57) * mm, "end": v(-10.56, -100.43) * mm});
            skLineSegment(sketch, "E34.29.7", {"start": v(-9.67, -91.97) * mm, "end": v(-10.56, -100.43) * mm, "construction": true});
            skLineSegment(sketch, "E34.30.0", {"start": v(-1.36, -92.48) * mm, "end": v(0, -92.48) * mm});
            skLineSegment(sketch, "E34.30.1", {"start": v(-1.36, -100.98) * mm, "end": v(0, -100.98) * mm});
            skLineSegment(sketch, "E34.30.2", {"start": v(-1.36, -92.48) * mm, "end": v(-1.36, -100.98) * mm});
            skLineSegment(sketch, "E34.30.3", {"start": v(-1.96, -96.73) * mm, "end": v(1.46, -96.73) * mm, "construction": true});
            skLineSegment(sketch, "E34.30.4", {"start": v(1.36, -92.48) * mm, "end": v(0, -92.48) * mm});
            skLineSegment(sketch, "E34.30.5", {"start": v(1.36, -92.48) * mm, "end": v(1.36, -100.98) * mm});
            skLineSegment(sketch, "E34.30.6", {"start": v(1.36, -100.98) * mm, "end": v(0, -100.98) * mm});
            skLineSegment(sketch, "E34.30.7", {"start": v(0, -92.48) * mm, "end": v(0, -100.98) * mm, "construction": true});
            skLineSegment(sketch, "E34.31.0", {"start": v(8.32, -92.12) * mm, "end": v(9.67, -91.97) * mm});
            skLineSegment(sketch, "E34.31.1", {"start": v(9.2, -100.57) * mm, "end": v(10.56, -100.43) * mm});
            skLineSegment(sketch, "E34.31.2", {"start": v(8.32, -92.12) * mm, "end": v(9.2, -100.57) * mm});
            skLineSegment(sketch, "E34.31.3", {"start": v(8.16, -96.4) * mm, "end": v(11.56, -96.05) * mm, "construction": true});
            skLineSegment(sketch, "E34.31.4", {"start": v(11.02, -91.83) * mm, "end": v(9.67, -91.97) * mm});
            skLineSegment(sketch, "E34.31.5", {"start": v(11.02, -91.83) * mm, "end": v(11.9, -100.28) * mm});
            skLineSegment(sketch, "E34.31.6", {"start": v(11.9, -100.28) * mm, "end": v(10.56, -100.43) * mm});
            skLineSegment(sketch, "E34.31.7", {"start": v(9.67, -91.97) * mm, "end": v(10.56, -100.43) * mm, "construction": true});
            skLineSegment(sketch, "E34.32.0", {"start": v(17.9, -90.74) * mm, "end": v(19.23, -90.46) * mm});
            skLineSegment(sketch, "E34.32.1", {"start": v(19.67, -99.06) * mm, "end": v(21, -98.77) * mm});
            skLineSegment(sketch, "E34.32.2", {"start": v(17.9, -90.74) * mm, "end": v(19.67, -99.06) * mm});
            skLineSegment(sketch, "E34.32.3", {"start": v(18.2, -95.02) * mm, "end": v(21.54, -94.31) * mm, "construction": true});
            skLineSegment(sketch, "E34.32.4", {"start": v(20.56, -90.18) * mm, "end": v(19.23, -90.46) * mm});
            skLineSegment(sketch, "E34.32.5", {"start": v(20.56, -90.18) * mm, "end": v(22.32, -98.5) * mm});
            skLineSegment(sketch, "E34.32.6", {"start": v(22.32, -98.5) * mm, "end": v(21, -98.77) * mm});
            skLineSegment(sketch, "E34.32.7", {"start": v(19.23, -90.46) * mm, "end": v(21, -98.77) * mm, "construction": true});
            skLineSegment(sketch, "E34.33.0", {"start": v(27.29, -88.37) * mm, "end": v(28.58, -87.95) * mm});
            skLineSegment(sketch, "E34.33.1", {"start": v(29.91, -96.46) * mm, "end": v(31.2, -96.04) * mm});
            skLineSegment(sketch, "E34.33.2", {"start": v(27.29, -88.37) * mm, "end": v(29.91, -96.46) * mm});
            skLineSegment(sketch, "E34.33.3", {"start": v(28.02, -92.6) * mm, "end": v(31.28, -91.54) * mm, "construction": true});
            skLineSegment(sketch, "E34.33.4", {"start": v(29.87, -87.53) * mm, "end": v(28.58, -87.95) * mm});
            skLineSegment(sketch, "E34.33.5", {"start": v(29.87, -87.53) * mm, "end": v(32.5, -95.62) * mm});
            skLineSegment(sketch, "E34.33.6", {"start": v(32.5, -95.62) * mm, "end": v(31.2, -96.04) * mm});
            skLineSegment(sketch, "E34.33.7", {"start": v(28.58, -87.95) * mm, "end": v(31.2, -96.04) * mm, "construction": true});
            skLineSegment(sketch, "E34.34.0", {"start": v(36.37, -85.04) * mm, "end": v(37.62, -84.48) * mm});
            skLineSegment(sketch, "E34.34.1", {"start": v(39.83, -92.8) * mm, "end": v(41.07, -92.25) * mm});
            skLineSegment(sketch, "E34.34.2", {"start": v(36.37, -85.04) * mm, "end": v(39.83, -92.8) * mm});
            skLineSegment(sketch, "E34.34.3", {"start": v(37.55, -89.17) * mm, "end": v(40.68, -87.77) * mm, "construction": true});
            skLineSegment(sketch, "E34.34.4", {"start": v(38.86, -83.93) * mm, "end": v(37.62, -84.48) * mm});
            skLineSegment(sketch, "E34.34.5", {"start": v(38.86, -83.93) * mm, "end": v(42.31, -91.7) * mm});
            skLineSegment(sketch, "E34.34.6", {"start": v(42.31, -91.7) * mm, "end": v(41.07, -92.25) * mm});
            skLineSegment(sketch, "E34.34.7", {"start": v(37.62, -84.48) * mm, "end": v(41.07, -92.25) * mm, "construction": true});
            skLineSegment(sketch, "E34.35.0", {"start": v(45.06, -80.77) * mm, "end": v(46.24, -80.1) * mm});
            skLineSegment(sketch, "E34.35.1", {"start": v(49.31, -88.13) * mm, "end": v(50.49, -87.45) * mm});
            skLineSegment(sketch, "E34.35.2", {"start": v(45.06, -80.77) * mm, "end": v(49.31, -88.13) * mm});
            skLineSegment(sketch, "E34.35.3", {"start": v(46.67, -84.75) * mm, "end": v(49.63, -83.04) * mm, "construction": true});
            skLineSegment(sketch, "E34.35.4", {"start": v(47.42, -79.41) * mm, "end": v(46.24, -80.1) * mm});
            skLineSegment(sketch, "E34.35.5", {"start": v(47.42, -79.41) * mm, "end": v(51.67, -86.77) * mm});
            skLineSegment(sketch, "E34.35.6", {"start": v(51.67, -86.77) * mm, "end": v(50.49, -87.45) * mm});
            skLineSegment(sketch, "E34.35.7", {"start": v(46.24, -80.1) * mm, "end": v(50.49, -87.45) * mm, "construction": true});
            skLineSegment(sketch, "E34.36.0", {"start": v(53.26, -75.62) * mm, "end": v(54.36, -74.82) * mm});
            skLineSegment(sketch, "E34.36.1", {"start": v(58.26, -82.5) * mm, "end": v(59.35, -81.7) * mm});
            skLineSegment(sketch, "E34.36.2", {"start": v(53.26, -75.62) * mm, "end": v(58.26, -82.5) * mm});
            skLineSegment(sketch, "E34.36.3", {"start": v(55.27, -79.4) * mm, "end": v(58.04, -77.4) * mm, "construction": true});
            skLineSegment(sketch, "E34.36.4", {"start": v(55.46, -74.02) * mm, "end": v(54.36, -74.82) * mm});
            skLineSegment(sketch, "E34.36.5", {"start": v(55.46, -74.02) * mm, "end": v(60.45, -80.9) * mm});
            skLineSegment(sketch, "E34.36.6", {"start": v(60.45, -80.9) * mm, "end": v(59.35, -81.7) * mm});
            skLineSegment(sketch, "E34.36.7", {"start": v(54.36, -74.82) * mm, "end": v(59.35, -81.7) * mm, "construction": true});
            skLineSegment(sketch, "E34.37.0", {"start": v(60.87, -69.63) * mm, "end": v(61.88, -68.73) * mm});
            skLineSegment(sketch, "E34.37.1", {"start": v(66.56, -75.95) * mm, "end": v(67.57, -75.04) * mm});
            skLineSegment(sketch, "E34.37.2", {"start": v(60.87, -69.63) * mm, "end": v(66.56, -75.95) * mm});
            skLineSegment(sketch, "E34.37.3", {"start": v(63.27, -73.2) * mm, "end": v(65.8, -70.9) * mm, "construction": true});
            skLineSegment(sketch, "E34.37.4", {"start": v(62.9, -67.82) * mm, "end": v(61.88, -68.73) * mm});
            skLineSegment(sketch, "E34.37.5", {"start": v(62.9, -67.82) * mm, "end": v(68.58, -74.13) * mm});
            skLineSegment(sketch, "E34.37.6", {"start": v(68.58, -74.13) * mm, "end": v(67.57, -75.04) * mm});
            skLineSegment(sketch, "E34.37.7", {"start": v(61.88, -68.73) * mm, "end": v(67.57, -75.04) * mm, "construction": true});
            skLineSegment(sketch, "E34.38.0", {"start": v(67.82, -62.9) * mm, "end": v(68.73, -61.88) * mm});
            skLineSegment(sketch, "E34.38.1", {"start": v(74.13, -68.58) * mm, "end": v(75.04, -67.57) * mm});
            skLineSegment(sketch, "E34.38.2", {"start": v(67.82, -62.9) * mm, "end": v(74.13, -68.58) * mm});
            skLineSegment(sketch, "E34.38.3", {"start": v(70.57, -66.18) * mm, "end": v(72.86, -63.64) * mm, "construction": true});
            skLineSegment(sketch, "E34.38.4", {"start": v(69.63, -60.87) * mm, "end": v(68.73, -61.88) * mm});
            skLineSegment(sketch, "E34.38.5", {"start": v(69.63, -60.87) * mm, "end": v(75.95, -66.56) * mm});
            skLineSegment(sketch, "E34.38.6", {"start": v(75.95, -66.56) * mm, "end": v(75.04, -67.57) * mm});
            skLineSegment(sketch, "E34.38.7", {"start": v(68.73, -61.88) * mm, "end": v(75.04, -67.57) * mm, "construction": true});
            skLineSegment(sketch, "E34.39.0", {"start": v(74.02, -55.46) * mm, "end": v(74.82, -54.36) * mm});
            skLineSegment(sketch, "E34.39.1", {"start": v(80.9, -60.45) * mm, "end": v(81.7, -59.35) * mm});
            skLineSegment(sketch, "E34.39.2", {"start": v(74.02, -55.46) * mm, "end": v(80.9, -60.45) * mm});
            skLineSegment(sketch, "E34.39.3", {"start": v(77.1, -58.44) * mm, "end": v(79.11, -55.68) * mm, "construction": true});
            skLineSegment(sketch, "E34.39.4", {"start": v(75.62, -53.26) * mm, "end": v(74.82, -54.36) * mm});
            skLineSegment(sketch, "E34.39.5", {"start": v(75.62, -53.26) * mm, "end": v(82.5, -58.26) * mm});
            skLineSegment(sketch, "E34.39.6", {"start": v(82.5, -58.26) * mm, "end": v(81.7, -59.35) * mm});
            skLineSegment(sketch, "E34.39.7", {"start": v(74.82, -54.36) * mm, "end": v(81.7, -59.35) * mm, "construction": true});
            skLineSegment(sketch, "E34.40.0", {"start": v(79.41, -47.42) * mm, "end": v(80.1, -46.24) * mm});
            skLineSegment(sketch, "E34.40.1", {"start": v(86.77, -51.67) * mm, "end": v(87.45, -50.5) * mm});
            skLineSegment(sketch, "E34.40.2", {"start": v(79.41, -47.42) * mm, "end": v(86.77, -51.67) * mm});
            skLineSegment(sketch, "E34.40.3", {"start": v(82.79, -50.06) * mm, "end": v(84.5, -47.1) * mm, "construction": true});
            skLineSegment(sketch, "E34.40.4", {"start": v(80.77, -45.06) * mm, "end": v(80.1, -46.24) * mm});
            skLineSegment(sketch, "E34.40.5", {"start": v(80.77, -45.06) * mm, "end": v(88.13, -49.31) * mm});
            skLineSegment(sketch, "E34.40.6", {"start": v(88.13, -49.31) * mm, "end": v(87.45, -50.5) * mm});
            skLineSegment(sketch, "E34.40.7", {"start": v(80.1, -46.24) * mm, "end": v(87.45, -50.5) * mm, "construction": true});
            skLineSegment(sketch, "E34.41.0", {"start": v(83.93, -38.86) * mm, "end": v(84.48, -37.62) * mm});
            skLineSegment(sketch, "E34.41.1", {"start": v(91.7, -42.31) * mm, "end": v(92.25, -41.07) * mm});
            skLineSegment(sketch, "E34.41.2", {"start": v(83.93, -38.86) * mm, "end": v(91.7, -42.31) * mm});
            skLineSegment(sketch, "E34.41.3", {"start": v(87.57, -41.14) * mm, "end": v(88.96, -38) * mm, "construction": true});
            skLineSegment(sketch, "E34.41.4", {"start": v(85.04, -36.37) * mm, "end": v(84.48, -37.62) * mm});
            skLineSegment(sketch, "E34.41.5", {"start": v(85.04, -36.37) * mm, "end": v(92.8, -39.83) * mm});
            skLineSegment(sketch, "E34.41.6", {"start": v(92.8, -39.83) * mm, "end": v(92.25, -41.07) * mm});
            skLineSegment(sketch, "E34.41.7", {"start": v(84.48, -37.62) * mm, "end": v(92.25, -41.07) * mm, "construction": true});
            skLineSegment(sketch, "E34.42.0", {"start": v(87.53, -29.87) * mm, "end": v(87.95, -28.58) * mm});
            skLineSegment(sketch, "E34.42.1", {"start": v(95.62, -32.5) * mm, "end": v(96.04, -31.2) * mm});
            skLineSegment(sketch, "E34.42.2", {"start": v(87.53, -29.87) * mm, "end": v(95.62, -32.5) * mm});
            skLineSegment(sketch, "E34.42.3", {"start": v(91.39, -31.76) * mm, "end": v(92.45, -28.5) * mm, "construction": true});
            skLineSegment(sketch, "E34.42.4", {"start": v(88.37, -27.29) * mm, "end": v(87.95, -28.58) * mm});
            skLineSegment(sketch, "E34.42.5", {"start": v(88.37, -27.29) * mm, "end": v(96.46, -29.91) * mm});
            skLineSegment(sketch, "E34.42.6", {"start": v(96.46, -29.91) * mm, "end": v(96.04, -31.2) * mm});
            skLineSegment(sketch, "E34.42.7", {"start": v(87.95, -28.58) * mm, "end": v(96.04, -31.2) * mm, "construction": true});
            skLineSegment(sketch, "E34.43.0", {"start": v(90.18, -20.56) * mm, "end": v(90.46, -19.23) * mm});
            skLineSegment(sketch, "E34.43.1", {"start": v(98.5, -22.32) * mm, "end": v(98.77, -21) * mm});
            skLineSegment(sketch, "E34.43.2", {"start": v(90.18, -20.56) * mm, "end": v(98.5, -22.32) * mm});
            skLineSegment(sketch, "E34.43.3", {"start": v(94.2, -22.03) * mm, "end": v(94.92, -18.68) * mm, "construction": true});
            skLineSegment(sketch, "E34.43.4", {"start": v(90.74, -17.9) * mm, "end": v(90.46, -19.23) * mm});
            skLineSegment(sketch, "E34.43.5", {"start": v(90.74, -17.9) * mm, "end": v(99.06, -19.67) * mm});
            skLineSegment(sketch, "E34.43.6", {"start": v(99.06, -19.67) * mm, "end": v(98.77, -21) * mm});
            skLineSegment(sketch, "E34.43.7", {"start": v(90.46, -19.23) * mm, "end": v(98.77, -21) * mm, "construction": true});
            skLineSegment(sketch, "E34.44.0", {"start": v(91.83, -11.02) * mm, "end": v(91.97, -9.67) * mm});
            skLineSegment(sketch, "E34.44.1", {"start": v(100.28, -11.9) * mm, "end": v(100.43, -10.56) * mm});
            skLineSegment(sketch, "E34.44.2", {"start": v(91.83, -11.02) * mm, "end": v(100.28, -11.9) * mm});
            skLineSegment(sketch, "E34.44.3", {"start": v(96, -12.06) * mm, "end": v(96.35, -8.66) * mm, "construction": true});
            skLineSegment(sketch, "E34.44.4", {"start": v(92.12, -8.32) * mm, "end": v(91.97, -9.67) * mm});
            skLineSegment(sketch, "E34.44.5", {"start": v(92.12, -8.32) * mm, "end": v(100.57, -9.2) * mm});
            skLineSegment(sketch, "E34.44.6", {"start": v(100.57, -9.2) * mm, "end": v(100.43, -10.56) * mm});
            skLineSegment(sketch, "E34.44.7", {"start": v(91.97, -9.67) * mm, "end": v(100.43, -10.56) * mm, "construction": true});
            skLineSegment(sketch, "E34.45.0", {"start": v(92.48, -1.36) * mm, "end": v(92.48, 0) * mm});
            skLineSegment(sketch, "E34.45.1", {"start": v(100.98, -1.36) * mm, "end": v(100.98, 0) * mm});
            skLineSegment(sketch, "E34.45.2", {"start": v(92.48, -1.36) * mm, "end": v(100.98, -1.36) * mm});
            skLineSegment(sketch, "E34.45.3", {"start": v(96.73, -1.96) * mm, "end": v(96.73, 1.46) * mm, "construction": true});
            skLineSegment(sketch, "E34.45.4", {"start": v(92.48, 1.36) * mm, "end": v(92.48, 0) * mm});
            skLineSegment(sketch, "E34.45.5", {"start": v(92.48, 1.36) * mm, "end": v(100.98, 1.36) * mm});
            skLineSegment(sketch, "E34.45.6", {"start": v(100.98, 1.36) * mm, "end": v(100.98, 0) * mm});
            skLineSegment(sketch, "E34.45.7", {"start": v(92.48, 0) * mm, "end": v(100.98, 0) * mm, "construction": true});
            skLineSegment(sketch, "E34.46.0", {"start": v(92.12, 8.32) * mm, "end": v(91.97, 9.67) * mm});
            skLineSegment(sketch, "E34.46.1", {"start": v(100.57, 9.2) * mm, "end": v(100.43, 10.56) * mm});
            skLineSegment(sketch, "E34.46.2", {"start": v(92.12, 8.32) * mm, "end": v(100.57, 9.2) * mm});
            skLineSegment(sketch, "E34.46.3", {"start": v(96.4, 8.16) * mm, "end": v(96.05, 11.56) * mm, "construction": true});
            skLineSegment(sketch, "E34.46.4", {"start": v(91.83, 11.02) * mm, "end": v(91.97, 9.67) * mm});
            skLineSegment(sketch, "E34.46.5", {"start": v(91.83, 11.02) * mm, "end": v(100.28, 11.9) * mm});
            skLineSegment(sketch, "E34.46.6", {"start": v(100.28, 11.9) * mm, "end": v(100.43, 10.56) * mm});
            skLineSegment(sketch, "E34.46.7", {"start": v(91.97, 9.67) * mm, "end": v(100.43, 10.56) * mm, "construction": true});
            skLineSegment(sketch, "E34.47.0", {"start": v(90.74, 17.9) * mm, "end": v(90.46, 19.23) * mm});
            skLineSegment(sketch, "E34.47.1", {"start": v(99.06, 19.67) * mm, "end": v(98.77, 21) * mm});
            skLineSegment(sketch, "E34.47.2", {"start": v(90.74, 17.9) * mm, "end": v(99.06, 19.67) * mm});
            skLineSegment(sketch, "E34.47.3", {"start": v(95.02, 18.2) * mm, "end": v(94.31, 21.54) * mm, "construction": true});
            skLineSegment(sketch, "E34.47.4", {"start": v(90.18, 20.56) * mm, "end": v(90.46, 19.23) * mm});
            skLineSegment(sketch, "E34.47.5", {"start": v(90.18, 20.56) * mm, "end": v(98.5, 22.32) * mm});
            skLineSegment(sketch, "E34.47.6", {"start": v(98.5, 22.32) * mm, "end": v(98.77, 21) * mm});
            skLineSegment(sketch, "E34.47.7", {"start": v(90.46, 19.23) * mm, "end": v(98.77, 21) * mm, "construction": true});
            skLineSegment(sketch, "E34.48.0", {"start": v(88.37, 27.29) * mm, "end": v(87.95, 28.58) * mm});
            skLineSegment(sketch, "E34.48.1", {"start": v(96.46, 29.91) * mm, "end": v(96.04, 31.2) * mm});
            skLineSegment(sketch, "E34.48.2", {"start": v(88.37, 27.29) * mm, "end": v(96.46, 29.91) * mm});
            skLineSegment(sketch, "E34.48.3", {"start": v(92.6, 28.02) * mm, "end": v(91.54, 31.28) * mm, "construction": true});
            skLineSegment(sketch, "E34.48.4", {"start": v(87.53, 29.87) * mm, "end": v(87.95, 28.58) * mm});
            skLineSegment(sketch, "E34.48.5", {"start": v(87.53, 29.87) * mm, "end": v(95.62, 32.5) * mm});
            skLineSegment(sketch, "E34.48.6", {"start": v(95.62, 32.5) * mm, "end": v(96.04, 31.2) * mm});
            skLineSegment(sketch, "E34.48.7", {"start": v(87.95, 28.58) * mm, "end": v(96.04, 31.2) * mm, "construction": true});
            skLineSegment(sketch, "E34.49.0", {"start": v(85.04, 36.37) * mm, "end": v(84.48, 37.62) * mm});
            skLineSegment(sketch, "E34.49.1", {"start": v(92.8, 39.83) * mm, "end": v(92.25, 41.07) * mm});
            skLineSegment(sketch, "E34.49.2", {"start": v(85.04, 36.37) * mm, "end": v(92.8, 39.83) * mm});
            skLineSegment(sketch, "E34.49.3", {"start": v(89.17, 37.55) * mm, "end": v(87.77, 40.68) * mm, "construction": true});
            skLineSegment(sketch, "E34.49.4", {"start": v(83.93, 38.86) * mm, "end": v(84.48, 37.62) * mm});
            skLineSegment(sketch, "E34.49.5", {"start": v(83.93, 38.86) * mm, "end": v(91.7, 42.31) * mm});
            skLineSegment(sketch, "E34.49.6", {"start": v(91.7, 42.31) * mm, "end": v(92.25, 41.07) * mm});
            skLineSegment(sketch, "E34.49.7", {"start": v(84.48, 37.62) * mm, "end": v(92.25, 41.07) * mm, "construction": true});
            skLineSegment(sketch, "E34.50.0", {"start": v(80.77, 45.06) * mm, "end": v(80.1, 46.24) * mm});
            skLineSegment(sketch, "E34.50.1", {"start": v(88.13, 49.31) * mm, "end": v(87.45, 50.49) * mm});
            skLineSegment(sketch, "E34.50.2", {"start": v(80.77, 45.06) * mm, "end": v(88.13, 49.31) * mm});
            skLineSegment(sketch, "E34.50.3", {"start": v(84.75, 46.67) * mm, "end": v(83.04, 49.63) * mm, "construction": true});
            skLineSegment(sketch, "E34.50.4", {"start": v(79.41, 47.42) * mm, "end": v(80.1, 46.24) * mm});
            skLineSegment(sketch, "E34.50.5", {"start": v(79.41, 47.42) * mm, "end": v(86.77, 51.67) * mm});
            skLineSegment(sketch, "E34.50.6", {"start": v(86.77, 51.67) * mm, "end": v(87.45, 50.49) * mm});
            skLineSegment(sketch, "E34.50.7", {"start": v(80.1, 46.24) * mm, "end": v(87.45, 50.49) * mm, "construction": true});
            skLineSegment(sketch, "E34.51.0", {"start": v(75.62, 53.26) * mm, "end": v(74.82, 54.36) * mm});
            skLineSegment(sketch, "E34.51.1", {"start": v(82.5, 58.26) * mm, "end": v(81.7, 59.35) * mm});
            skLineSegment(sketch, "E34.51.2", {"start": v(75.62, 53.26) * mm, "end": v(82.5, 58.26) * mm});
            skLineSegment(sketch, "E34.51.3", {"start": v(79.4, 55.27) * mm, "end": v(77.4, 58.04) * mm, "construction": true});
            skLineSegment(sketch, "E34.51.4", {"start": v(74.02, 55.46) * mm, "end": v(74.82, 54.36) * mm});
            skLineSegment(sketch, "E34.51.5", {"start": v(74.02, 55.46) * mm, "end": v(80.9, 60.45) * mm});
            skLineSegment(sketch, "E34.51.6", {"start": v(80.9, 60.45) * mm, "end": v(81.7, 59.35) * mm});
            skLineSegment(sketch, "E34.51.7", {"start": v(74.82, 54.36) * mm, "end": v(81.7, 59.35) * mm, "construction": true});
            skLineSegment(sketch, "E34.52.0", {"start": v(69.63, 60.87) * mm, "end": v(68.73, 61.88) * mm});
            skLineSegment(sketch, "E34.52.1", {"start": v(75.95, 66.56) * mm, "end": v(75.04, 67.57) * mm});
            skLineSegment(sketch, "E34.52.2", {"start": v(69.63, 60.87) * mm, "end": v(75.95, 66.56) * mm});
            skLineSegment(sketch, "E34.52.3", {"start": v(73.2, 63.27) * mm, "end": v(70.9, 65.8) * mm, "construction": true});
            skLineSegment(sketch, "E34.52.4", {"start": v(67.82, 62.9) * mm, "end": v(68.73, 61.88) * mm});
            skLineSegment(sketch, "E34.52.5", {"start": v(67.82, 62.9) * mm, "end": v(74.13, 68.58) * mm});
            skLineSegment(sketch, "E34.52.6", {"start": v(74.13, 68.58) * mm, "end": v(75.04, 67.57) * mm});
            skLineSegment(sketch, "E34.52.7", {"start": v(68.73, 61.88) * mm, "end": v(75.04, 67.57) * mm, "construction": true});
            skLineSegment(sketch, "E34.53.0", {"start": v(62.9, 67.82) * mm, "end": v(61.88, 68.73) * mm});
            skLineSegment(sketch, "E34.53.1", {"start": v(68.58, 74.13) * mm, "end": v(67.57, 75.04) * mm});
            skLineSegment(sketch, "E34.53.2", {"start": v(62.9, 67.82) * mm, "end": v(68.58, 74.13) * mm});
            skLineSegment(sketch, "E34.53.3", {"start": v(66.18, 70.57) * mm, "end": v(63.64, 72.86) * mm, "construction": true});
            skLineSegment(sketch, "E34.53.4", {"start": v(60.87, 69.63) * mm, "end": v(61.88, 68.73) * mm});
            skLineSegment(sketch, "E34.53.5", {"start": v(60.87, 69.63) * mm, "end": v(66.56, 75.95) * mm});
            skLineSegment(sketch, "E34.53.6", {"start": v(66.56, 75.95) * mm, "end": v(67.57, 75.04) * mm});
            skLineSegment(sketch, "E34.53.7", {"start": v(61.88, 68.73) * mm, "end": v(67.57, 75.04) * mm, "construction": true});
            skLineSegment(sketch, "E34.54.0", {"start": v(55.46, 74.02) * mm, "end": v(54.36, 74.82) * mm});
            skLineSegment(sketch, "E34.54.1", {"start": v(60.45, 80.9) * mm, "end": v(59.35, 81.7) * mm});
            skLineSegment(sketch, "E34.54.2", {"start": v(55.46, 74.02) * mm, "end": v(60.45, 80.9) * mm});
            skLineSegment(sketch, "E34.54.3", {"start": v(58.44, 77.1) * mm, "end": v(55.68, 79.11) * mm, "construction": true});
            skLineSegment(sketch, "E34.54.4", {"start": v(53.26, 75.62) * mm, "end": v(54.36, 74.82) * mm});
            skLineSegment(sketch, "E34.54.5", {"start": v(53.26, 75.62) * mm, "end": v(58.26, 82.5) * mm});
            skLineSegment(sketch, "E34.54.6", {"start": v(58.26, 82.5) * mm, "end": v(59.35, 81.7) * mm});
            skLineSegment(sketch, "E34.54.7", {"start": v(54.36, 74.82) * mm, "end": v(59.35, 81.7) * mm, "construction": true});
            skLineSegment(sketch, "E34.55.0", {"start": v(47.42, 79.41) * mm, "end": v(46.24, 80.1) * mm});
            skLineSegment(sketch, "E34.55.1", {"start": v(51.67, 86.77) * mm, "end": v(50.49, 87.45) * mm});
            skLineSegment(sketch, "E34.55.2", {"start": v(47.42, 79.41) * mm, "end": v(51.67, 86.77) * mm});
            skLineSegment(sketch, "E34.55.3", {"start": v(50.06, 82.79) * mm, "end": v(47.1, 84.5) * mm, "construction": true});
            skLineSegment(sketch, "E34.55.4", {"start": v(45.06, 80.77) * mm, "end": v(46.24, 80.1) * mm});
            skLineSegment(sketch, "E34.55.5", {"start": v(45.06, 80.77) * mm, "end": v(49.31, 88.13) * mm});
            skLineSegment(sketch, "E34.55.6", {"start": v(49.31, 88.13) * mm, "end": v(50.49, 87.45) * mm});
            skLineSegment(sketch, "E34.55.7", {"start": v(46.24, 80.1) * mm, "end": v(50.49, 87.45) * mm, "construction": true});
            skLineSegment(sketch, "E34.56.0", {"start": v(38.86, 83.93) * mm, "end": v(37.62, 84.48) * mm});
            skLineSegment(sketch, "E34.56.1", {"start": v(42.31, 91.7) * mm, "end": v(41.07, 92.25) * mm});
            skLineSegment(sketch, "E34.56.2", {"start": v(38.86, 83.93) * mm, "end": v(42.31, 91.7) * mm});
            skLineSegment(sketch, "E34.56.3", {"start": v(41.14, 87.57) * mm, "end": v(38, 88.96) * mm, "construction": true});
            skLineSegment(sketch, "E34.56.4", {"start": v(36.37, 85.04) * mm, "end": v(37.62, 84.48) * mm});
            skLineSegment(sketch, "E34.56.5", {"start": v(36.37, 85.04) * mm, "end": v(39.83, 92.8) * mm});
            skLineSegment(sketch, "E34.56.6", {"start": v(39.83, 92.8) * mm, "end": v(41.07, 92.25) * mm});
            skLineSegment(sketch, "E34.56.7", {"start": v(37.62, 84.48) * mm, "end": v(41.07, 92.25) * mm, "construction": true});
            skLineSegment(sketch, "E34.57.0", {"start": v(29.87, 87.53) * mm, "end": v(28.58, 87.95) * mm});
            skLineSegment(sketch, "E34.57.1", {"start": v(32.5, 95.62) * mm, "end": v(31.2, 96.04) * mm});
            skLineSegment(sketch, "E34.57.2", {"start": v(29.87, 87.53) * mm, "end": v(32.5, 95.62) * mm});
            skLineSegment(sketch, "E34.57.3", {"start": v(31.76, 91.39) * mm, "end": v(28.5, 92.45) * mm, "construction": true});
            skLineSegment(sketch, "E34.57.4", {"start": v(27.29, 88.37) * mm, "end": v(28.58, 87.95) * mm});
            skLineSegment(sketch, "E34.57.5", {"start": v(27.29, 88.37) * mm, "end": v(29.91, 96.46) * mm});
            skLineSegment(sketch, "E34.57.6", {"start": v(29.91, 96.46) * mm, "end": v(31.2, 96.04) * mm});
            skLineSegment(sketch, "E34.57.7", {"start": v(28.58, 87.95) * mm, "end": v(31.2, 96.04) * mm, "construction": true});
            skLineSegment(sketch, "E34.58.0", {"start": v(20.56, 90.18) * mm, "end": v(19.23, 90.46) * mm});
            skLineSegment(sketch, "E34.58.1", {"start": v(22.32, 98.5) * mm, "end": v(21, 98.77) * mm});
            skLineSegment(sketch, "E34.58.2", {"start": v(20.56, 90.18) * mm, "end": v(22.32, 98.5) * mm});
            skLineSegment(sketch, "E34.58.3", {"start": v(22.03, 94.2) * mm, "end": v(18.68, 94.92) * mm, "construction": true});
            skLineSegment(sketch, "E34.58.4", {"start": v(17.9, 90.74) * mm, "end": v(19.23, 90.46) * mm});
            skLineSegment(sketch, "E34.58.5", {"start": v(17.9, 90.74) * mm, "end": v(19.67, 99.06) * mm});
            skLineSegment(sketch, "E34.58.6", {"start": v(19.67, 99.06) * mm, "end": v(21, 98.77) * mm});
            skLineSegment(sketch, "E34.58.7", {"start": v(19.23, 90.46) * mm, "end": v(21, 98.77) * mm, "construction": true});
            skLineSegment(sketch, "E34.59.0", {"start": v(11.02, 91.83) * mm, "end": v(9.67, 91.97) * mm});
            skLineSegment(sketch, "E34.59.1", {"start": v(11.9, 100.28) * mm, "end": v(10.56, 100.43) * mm});
            skLineSegment(sketch, "E34.59.2", {"start": v(11.02, 91.83) * mm, "end": v(11.9, 100.28) * mm});
            skLineSegment(sketch, "E34.59.3", {"start": v(12.06, 96) * mm, "end": v(8.66, 96.35) * mm, "construction": true});
            skLineSegment(sketch, "E34.59.4", {"start": v(8.32, 92.12) * mm, "end": v(9.67, 91.97) * mm});
            skLineSegment(sketch, "E34.59.5", {"start": v(8.32, 92.12) * mm, "end": v(9.2, 100.57) * mm});
            skLineSegment(sketch, "E34.59.6", {"start": v(9.2, 100.57) * mm, "end": v(10.56, 100.43) * mm});
            skLineSegment(sketch, "E34.59.7", {"start": v(9.67, 91.97) * mm, "end": v(10.56, 100.43) * mm, "construction": true});
            skPoint(sketch, "E34.center", {"position": v(0, 0) * mm});
            skSolve(sketch);
        }
        {
            var Q0;
            Q0=qSketchRegion(id+"F13",true);
            extrude(context, id + "F14", {"entities" : qUnion([Q0]), "operationType" : NewBodyOperationType.REMOVE, "depth" : 25 * mm, "offsetDistance" : 25 * mm, "hasSecondDirection" : true, "secondDirectionOppositeDirection" : false, "secondDirectionDepth" : 2 * mm});
        }
        {
            var Q0;
            Q0=makeQuery(id+"F1.opRevolve","SWEPT_FACE",FACE,{"disambiguationData":[OSD([sQuery(id+"F0.wireOp",EDGE,"E5")])]});
            var sketch = newSketch(context, id + "F15", { "sketchPlane" : qUnion([Q0])});
            skLineSegment(sketch, "E35", {"start": v(0, 0) * mm, "end": v(25.68, 95.85) * mm, "construction": true});
            skLineSegment(sketch, "E36", {"start": v(0, 0) * mm, "end": v(70.17, 70.17) * mm, "construction": true});
            skLineSegment(sketch, "E37", {"start": v(0, 0) * mm, "end": v(95.85, 25.68) * mm, "construction": true});
            skLineSegment(sketch, "E38", {"start": v(0, 0) * mm, "end": v(95.85, -25.68) * mm, "construction": true});
            skLineSegment(sketch, "E39", {"start": v(0, 0) * mm, "end": v(70.17, -70.17) * mm, "construction": true});
            skLineSegment(sketch, "E40", {"start": v(0, 0) * mm, "end": v(25.68, -95.85) * mm, "construction": true});
            skLineSegment(sketch, "E41", {"start": v(0, 0) * mm, "end": v(104.73, 0) * mm, "construction": true});
            skArc(sketch, "E42", {"start": v(22.25, -102.34) * mm, "mid": v(27.1, -101.16) * mm, "end": v(31.9, -99.75) * mm});
            skArc(sketch, "E43", {"start": v(21.47, -99.44) * mm, "mid": v(26.33, -98.26) * mm, "end": v(31.13, -96.85) * mm});
            skLineSegment(sketch, "E44", {"start": v(25.68, 95.85) * mm, "end": v(30.51, 94.55) * mm, "construction": true});
            skLineSegment(sketch, "E45.MirrorCS", {"start": v(25.68, 95.85) * mm, "end": v(20.85, 97.14) * mm, "construction": true});
            skLineSegment(sketch, "E46", {"start": v(21.47, 99.44) * mm, "end": v(22.25, 102.34) * mm});
            skLineSegment(sketch, "E47", {"start": v(31.13, 96.85) * mm, "end": v(31.9, 99.75) * mm});
            skLineSegment(sketch, "E48", {"start": v(70.17, 70.17) * mm, "end": v(73.7, 66.63) * mm, "construction": true});
            skLineSegment(sketch, "E49.MirrorCS", {"start": v(70.17, 70.17) * mm, "end": v(66.63, 73.7) * mm, "construction": true});
            skLineSegment(sketch, "E50", {"start": v(75.38, 68.31) * mm, "end": v(77.5, 70.44) * mm});
            skLineSegment(sketch, "E51", {"start": v(68.31, 75.38) * mm, "end": v(70.44, 77.5) * mm});
            skArc(sketch, "E52.trimOffspring", {"start": v(31.9, 99.75) * mm, "mid": v(27.1, 101.16) * mm, "end": v(22.25, 102.34) * mm});
            skArc(sketch, "E53.trimOffspring", {"start": v(31.13, 96.85) * mm, "mid": v(26.33, 98.26) * mm, "end": v(21.47, 99.44) * mm});
            skLineSegment(sketch, "E54", {"start": v(95.85, 25.68) * mm, "end": v(97.14, 20.85) * mm, "construction": true});
            skLineSegment(sketch, "E55.MirrorCS", {"start": v(95.85, 25.68) * mm, "end": v(94.55, 30.51) * mm, "construction": true});
            skLineSegment(sketch, "E56", {"start": v(96.85, 31.13) * mm, "end": v(99.75, 31.9) * mm});
            skLineSegment(sketch, "E57", {"start": v(99.44, 21.47) * mm, "end": v(102.34, 22.25) * mm});
            skArc(sketch, "E58.trimOffspring", {"start": v(75.38, 68.31) * mm, "mid": v(71.93, 71.93) * mm, "end": v(68.31, 75.38) * mm});
            skArc(sketch, "E59.trimOffspring", {"start": v(77.5, 70.44) * mm, "mid": v(74.06, 74.06) * mm, "end": v(70.44, 77.5) * mm});
            skLineSegment(sketch, "E60", {"start": v(95.85, -25.68) * mm, "end": v(94.55, -30.51) * mm, "construction": true});
            skLineSegment(sketch, "E61.MirrorCS", {"start": v(95.85, -25.68) * mm, "end": v(97.14, -20.85) * mm, "construction": true});
            skLineSegment(sketch, "E62", {"start": v(96.85, -31.13) * mm, "end": v(99.75, -31.9) * mm});
            skLineSegment(sketch, "E63", {"start": v(99.44, -21.47) * mm, "end": v(102.34, -22.25) * mm});
            skArc(sketch, "E64.trimOffspring", {"start": v(99.44, 21.47) * mm, "mid": v(98.26, 26.33) * mm, "end": v(96.85, 31.13) * mm});
            skArc(sketch, "E65.trimOffspring", {"start": v(102.34, 22.25) * mm, "mid": v(101.16, 27.1) * mm, "end": v(99.75, 31.9) * mm});
            skLineSegment(sketch, "E66", {"start": v(70.17, -70.17) * mm, "end": v(66.63, -73.7) * mm, "construction": true});
            skLineSegment(sketch, "E67.MirrorCS", {"start": v(70.17, -70.17) * mm, "end": v(73.7, -66.63) * mm, "construction": true});
            skLineSegment(sketch, "E68", {"start": v(75.38, -68.31) * mm, "end": v(77.5, -70.44) * mm});
            skLineSegment(sketch, "E69", {"start": v(68.31, -75.38) * mm, "end": v(70.44, -77.5) * mm});
            skArc(sketch, "E70.trimOffspring", {"start": v(99.75, -31.9) * mm, "mid": v(101.16, -27.1) * mm, "end": v(102.34, -22.25) * mm});
            skArc(sketch, "E71.trimOffspring", {"start": v(96.85, -31.13) * mm, "mid": v(98.26, -26.33) * mm, "end": v(99.44, -21.47) * mm});
            skLineSegment(sketch, "E72", {"start": v(25.68, -95.85) * mm, "end": v(20.85, -97.14) * mm, "construction": true});
            skLineSegment(sketch, "E73.MirrorCS", {"start": v(25.68, -95.85) * mm, "end": v(30.51, -94.55) * mm, "construction": true});
            skLineSegment(sketch, "E74", {"start": v(31.13, -96.85) * mm, "end": v(31.9, -99.75) * mm});
            skLineSegment(sketch, "E75", {"start": v(21.47, -99.44) * mm, "end": v(22.25, -102.34) * mm});
            skArc(sketch, "E76.trimOffspring", {"start": v(68.31, -75.38) * mm, "mid": v(71.93, -71.93) * mm, "end": v(75.38, -68.31) * mm});
            skArc(sketch, "E77.trimOffspring", {"start": v(70.44, -77.5) * mm, "mid": v(74.06, -74.06) * mm, "end": v(77.5, -70.44) * mm});
            skSolve(sketch);
        }
        {
            var Q0;
            Q0=makeQuery(id+"F15.imprint","IMPRINT",FACE,{"disambiguationData":[TD([[makeQuery(id+"F15.imprint","IMPRINT",EDGE,{"derivedFrom":sQuery(id+"F15.wireOp",EDGE,"E42")}),1.0]])]});
            var Q1;
            Q1=makeQuery(id+"F15.imprint","IMPRINT",FACE,{"disambiguationData":[TD([[makeQuery(id+"F15.imprint","IMPRINT",EDGE,{"derivedFrom":sQuery(id+"F15.wireOp",EDGE,"E68")}),-1.0]])]});
            var Q2;
            Q2=makeQuery(id+"F15.imprint","IMPRINT",FACE,{"disambiguationData":[TD([[makeQuery(id+"F15.imprint","IMPRINT",EDGE,{"derivedFrom":sQuery(id+"F15.wireOp",EDGE,"E62")}),1.0]])]});
            var Q3;
            Q3=makeQuery(id+"F15.imprint","IMPRINT",FACE,{"disambiguationData":[TD([[makeQuery(id+"F15.imprint","IMPRINT",EDGE,{"derivedFrom":sQuery(id+"F15.wireOp",EDGE,"E56")}),-1.0]])]});
            var Q4;
            Q4=makeQuery(id+"F15.imprint","IMPRINT",FACE,{"disambiguationData":[TD([[makeQuery(id+"F15.imprint","IMPRINT",EDGE,{"derivedFrom":sQuery(id+"F15.wireOp",EDGE,"E50")}),1.0]])]});
            var Q5;
            Q5=makeQuery(id+"F15.imprint","IMPRINT",FACE,{"disambiguationData":[TD([[makeQuery(id+"F15.imprint","IMPRINT",EDGE,{"derivedFrom":sQuery(id+"F15.wireOp",EDGE,"E46")}),-1.0]])]});
            extrude(context, id + "F16", {"entities" : qUnion([Q0, Q1, Q2, Q3, Q4, Q5]), "operationType" : NewBodyOperationType.ADD, "depth" : 5 * mm, "offsetDistance" : 25 * mm});
        }
        {
            var Q0;
            Q0=makeQuery(id+"F16.opExtrude","CAP_FACE",FACE,{"disambiguationData":[OSD([sQuery(id+"F15.wireOp",EDGE,"E42"),sQuery(id+"F15.wireOp",EDGE,"E43"),sQuery(id+"F15.wireOp",EDGE,"E74"),sQuery(id+"F15.wireOp",EDGE,"E75")])],"isStart":false});
            var sketch = newSketch(context, id + "F17", { "sketchPlane" : qUnion([Q0])});
            skLineSegment(sketch, "E78", {"start": v(27.24, -101.64) * mm, "end": v(26.2, -97.78) * mm});
            skLineSegment(sketch, "E79", {"start": v(26.2, -97.78) * mm, "end": v(27.17, -97.52) * mm});
            skLineSegment(sketch, "E80", {"start": v(27.17, -97.52) * mm, "end": v(28.2, -101.39) * mm});
            skLineSegment(sketch, "E81", {"start": v(28.2, -101.39) * mm, "end": v(27.24, -101.64) * mm});
            skLineSegment(sketch, "E82.1.0", {"start": v(75.12, -73.7) * mm, "end": v(74.4, -74.4) * mm});
            skLineSegment(sketch, "E82.1.1", {"start": v(72.29, -70.87) * mm, "end": v(75.12, -73.7) * mm});
            skLineSegment(sketch, "E82.1.2", {"start": v(71.58, -71.58) * mm, "end": v(72.29, -70.87) * mm});
            skLineSegment(sketch, "E82.1.3", {"start": v(74.4, -74.4) * mm, "end": v(71.58, -71.58) * mm});
            skLineSegment(sketch, "E82.2.0", {"start": v(101.9, -26.27) * mm, "end": v(101.64, -27.24) * mm});
            skLineSegment(sketch, "E82.2.1", {"start": v(98.04, -25.23) * mm, "end": v(101.9, -26.27) * mm});
            skLineSegment(sketch, "E82.2.2", {"start": v(97.78, -26.2) * mm, "end": v(98.04, -25.23) * mm});
            skLineSegment(sketch, "E82.2.3", {"start": v(101.64, -27.24) * mm, "end": v(97.78, -26.2) * mm});
            skLineSegment(sketch, "E82.3.0", {"start": v(101.39, 28.2) * mm, "end": v(101.64, 27.24) * mm});
            skLineSegment(sketch, "E82.3.1", {"start": v(97.52, 27.17) * mm, "end": v(101.39, 28.2) * mm});
            skLineSegment(sketch, "E82.3.2", {"start": v(97.78, 26.2) * mm, "end": v(97.52, 27.17) * mm});
            skLineSegment(sketch, "E82.3.3", {"start": v(101.64, 27.24) * mm, "end": v(97.78, 26.2) * mm});
            skLineSegment(sketch, "E82.4.0", {"start": v(73.7, 75.12) * mm, "end": v(74.4, 74.4) * mm});
            skLineSegment(sketch, "E82.4.1", {"start": v(70.87, 72.29) * mm, "end": v(73.7, 75.12) * mm});
            skLineSegment(sketch, "E82.4.2", {"start": v(71.58, 71.58) * mm, "end": v(70.87, 72.29) * mm});
            skLineSegment(sketch, "E82.4.3", {"start": v(74.4, 74.4) * mm, "end": v(71.58, 71.58) * mm});
            skLineSegment(sketch, "E82.5.0", {"start": v(26.27, 101.9) * mm, "end": v(27.24, 101.64) * mm});
            skLineSegment(sketch, "E82.5.1", {"start": v(25.23, 98.04) * mm, "end": v(26.27, 101.9) * mm});
            skLineSegment(sketch, "E82.5.2", {"start": v(26.2, 97.78) * mm, "end": v(25.23, 98.04) * mm});
            skLineSegment(sketch, "E82.5.3", {"start": v(27.24, 101.64) * mm, "end": v(26.2, 97.78) * mm});
            skLineSegment(sketch, "E82.6.0", {"start": v(-28.2, 101.39) * mm, "end": v(-27.24, 101.64) * mm});
            skLineSegment(sketch, "E82.6.1", {"start": v(-27.17, 97.52) * mm, "end": v(-28.2, 101.39) * mm});
            skLineSegment(sketch, "E82.6.2", {"start": v(-26.2, 97.78) * mm, "end": v(-27.17, 97.52) * mm});
            skLineSegment(sketch, "E82.6.3", {"start": v(-27.24, 101.64) * mm, "end": v(-26.2, 97.78) * mm});
            skLineSegment(sketch, "E82.7.0", {"start": v(-75.12, 73.7) * mm, "end": v(-74.4, 74.4) * mm});
            skLineSegment(sketch, "E82.7.1", {"start": v(-72.29, 70.87) * mm, "end": v(-75.12, 73.7) * mm});
            skLineSegment(sketch, "E82.7.2", {"start": v(-71.58, 71.58) * mm, "end": v(-72.29, 70.87) * mm});
            skLineSegment(sketch, "E82.7.3", {"start": v(-74.4, 74.4) * mm, "end": v(-71.58, 71.58) * mm});
            skLineSegment(sketch, "E82.8.0", {"start": v(-101.9, 26.27) * mm, "end": v(-101.64, 27.24) * mm});
            skLineSegment(sketch, "E82.8.1", {"start": v(-98.04, 25.23) * mm, "end": v(-101.9, 26.27) * mm});
            skLineSegment(sketch, "E82.8.2", {"start": v(-97.78, 26.2) * mm, "end": v(-98.04, 25.23) * mm});
            skLineSegment(sketch, "E82.8.3", {"start": v(-101.64, 27.24) * mm, "end": v(-97.78, 26.2) * mm});
            skLineSegment(sketch, "E82.9.0", {"start": v(-101.39, -28.2) * mm, "end": v(-101.64, -27.24) * mm});
            skLineSegment(sketch, "E82.9.1", {"start": v(-97.52, -27.17) * mm, "end": v(-101.39, -28.2) * mm});
            skLineSegment(sketch, "E82.9.2", {"start": v(-97.78, -26.2) * mm, "end": v(-97.52, -27.17) * mm});
            skLineSegment(sketch, "E82.9.3", {"start": v(-101.64, -27.24) * mm, "end": v(-97.78, -26.2) * mm});
            skLineSegment(sketch, "E82.10.0", {"start": v(-73.7, -75.12) * mm, "end": v(-74.4, -74.4) * mm});
            skLineSegment(sketch, "E82.10.1", {"start": v(-70.87, -72.29) * mm, "end": v(-73.7, -75.12) * mm});
            skLineSegment(sketch, "E82.10.2", {"start": v(-71.58, -71.58) * mm, "end": v(-70.87, -72.29) * mm});
            skLineSegment(sketch, "E82.10.3", {"start": v(-74.4, -74.4) * mm, "end": v(-71.58, -71.58) * mm});
            skLineSegment(sketch, "E82.11.0", {"start": v(-26.27, -101.9) * mm, "end": v(-27.24, -101.64) * mm});
            skLineSegment(sketch, "E82.11.1", {"start": v(-25.23, -98.04) * mm, "end": v(-26.27, -101.9) * mm});
            skLineSegment(sketch, "E82.11.2", {"start": v(-26.2, -97.78) * mm, "end": v(-25.23, -98.04) * mm});
            skLineSegment(sketch, "E82.11.3", {"start": v(-27.24, -101.64) * mm, "end": v(-26.2, -97.78) * mm});
            skPoint(sketch, "E82.center", {"position": v(0, 0) * mm});
            skSolve(sketch);
        }
        {
            var Q0;
            {var subQ5=makeQuery(id+"F16.opExtrude","CAP_EDGE",EDGE,{"disambiguationData":[OSD([sQuery(id+"F15.wireOp",EDGE,"E74")])],"isStart":false});Q0=makeQuery(id+"F17.imprint","IMPRINT",FACE,{"disambiguationData":[TD([[makeQuery(id+"F17.imprint","IMPRINT",EDGE,{"derivedFrom":subQ5}),-1.0]])]});}
            var Q1;
            {var subQ0=sQuery(id+"F17.wireOp",EDGE,"E78");var subQ1=makeQuery(id+"F16.opExtrude","CAP_EDGE",EDGE,{"disambiguationData":[OSD([sQuery(id+"F15.wireOp",EDGE,"E42")])],"isStart":false});var subQ2=makeQuery(id+"F17.imprint","INTERSECT",VERTEX,{"derivedFrom":[subQ1,subQ0]});Q1=makeQuery(id+"F17.imprint","IMPRINT",FACE,{"disambiguationData":[TD([[makeQuery(id+"F17.imprint","IMPRINT",EDGE,{"disambiguationData":[TD([[subQ2,-1.0]])],"derivedFrom":subQ0}),-1.0]])]});}
            var Q2;
            {var subQ5=makeQuery(id+"F16.opExtrude","CAP_EDGE",EDGE,{"disambiguationData":[OSD([sQuery(id+"F15.wireOp",EDGE,"E75")])],"isStart":false});Q2=makeQuery(id+"F17.imprint","IMPRINT",FACE,{"disambiguationData":[TD([[makeQuery(id+"F17.imprint","IMPRINT",EDGE,{"derivedFrom":subQ5}),1.0]])]});}
            extrude(context, id + "F18", {"entities" : qUnion([Q0, Q1, Q2]), "operationType" : NewBodyOperationType.ADD, "depth" : 5 * mm, "offsetDistance" : 25 * mm});
        }
        {
            var Q0;
            Q0=makeQuery(id+"F16.opExtrude","CAP_FACE",FACE,{"disambiguationData":[OSD([sQuery(id+"F15.wireOp",EDGE,"E68"),sQuery(id+"F15.wireOp",EDGE,"E69"),sQuery(id+"F15.wireOp",EDGE,"E76.trimOffspring"),sQuery(id+"F15.wireOp",EDGE,"E77.trimOffspring")])],"isStart":false});
            extrude(context, id + "F19", {"entities" : qUnion([Q0]), "operationType" : NewBodyOperationType.ADD, "depth" : 5 * mm, "offsetDistance" : 25 * mm});
        }
        {
            var Q0;
            Q0=makeQuery(id+"F16.opExtrude","CAP_FACE",FACE,{"disambiguationData":[OSD([sQuery(id+"F15.wireOp",EDGE,"E62"),sQuery(id+"F15.wireOp",EDGE,"E63"),sQuery(id+"F15.wireOp",EDGE,"E70.trimOffspring"),sQuery(id+"F15.wireOp",EDGE,"E71.trimOffspring")])],"isStart":false});
            extrude(context, id + "F20", {"entities" : qUnion([Q0]), "operationType" : NewBodyOperationType.ADD, "depth" : 5 * mm, "offsetDistance" : 25 * mm});
        }
        {
            var Q0;
            Q0=makeQuery(id+"F16.opExtrude","CAP_FACE",FACE,{"disambiguationData":[OSD([sQuery(id+"F15.wireOp",EDGE,"E56"),sQuery(id+"F15.wireOp",EDGE,"E57"),sQuery(id+"F15.wireOp",EDGE,"E64.trimOffspring"),sQuery(id+"F15.wireOp",EDGE,"E65.trimOffspring")])],"isStart":false});
            extrude(context, id + "F21", {"entities" : qUnion([Q0]), "operationType" : NewBodyOperationType.ADD, "depth" : 5 * mm, "offsetDistance" : 25 * mm});
        }
        {
            var Q0;
            Q0=makeQuery(id+"F16.opExtrude","CAP_FACE",FACE,{"disambiguationData":[OSD([sQuery(id+"F15.wireOp",EDGE,"E50"),sQuery(id+"F15.wireOp",EDGE,"E51"),sQuery(id+"F15.wireOp",EDGE,"E58.trimOffspring"),sQuery(id+"F15.wireOp",EDGE,"E59.trimOffspring")])],"isStart":false});
            extrude(context, id + "F22", {"entities" : qUnion([Q0]), "operationType" : NewBodyOperationType.ADD, "depth" : 5 * mm, "offsetDistance" : 25 * mm});
        }
        {
            var Q0;
            Q0=makeQuery(id+"F16.opExtrude","CAP_FACE",FACE,{"disambiguationData":[OSD([sQuery(id+"F15.wireOp",EDGE,"E46"),sQuery(id+"F15.wireOp",EDGE,"E47"),sQuery(id+"F15.wireOp",EDGE,"E52.trimOffspring"),sQuery(id+"F15.wireOp",EDGE,"E53.trimOffspring")])],"isStart":false});
            extrude(context, id + "F23", {"entities" : qUnion([Q0]), "operationType" : NewBodyOperationType.ADD, "depth" : 5 * mm, "offsetDistance" : 25 * mm});
        }
        {
            var Q0;
            Q0=makeQuery(id+"F17.imprint","IMPRINT",FACE,{"disambiguationData":[TD([[makeQuery(id+"F17.imprint","IMPRINT",EDGE,{"derivedFrom":sQuery(id+"F17.wireOp",EDGE,"E82.5.0")}),-1.0]])]});
            var Q1;
            Q1=sQuery(id+"F17.wireOp",EDGE,"E82.5.3");
            revolve(context, id + "F24", {"operationType" : NewBodyOperationType.REMOVE, "surfaceOperationType" : NewSurfaceOperationType.NEW, "entities" : qUnion([Q0]), "axis" : qUnion([Q1]), "revolveType" : RevolveType.FULL, "oppositeDirection" : true});
        }
        {
            var Q0;
            Q0=makeQuery(id+"F17.imprint","IMPRINT",FACE,{"disambiguationData":[TD([[makeQuery(id+"F17.imprint","IMPRINT",EDGE,{"derivedFrom":sQuery(id+"F17.wireOp",EDGE,"E82.4.0")}),-1.0]])]});
            var Q1;
            Q1=sQuery(id+"F17.wireOp",EDGE,"E82.4.3");
            revolve(context, id + "F25", {"operationType" : NewBodyOperationType.REMOVE, "surfaceOperationType" : NewSurfaceOperationType.NEW, "entities" : qUnion([Q0]), "axis" : qUnion([Q1]), "revolveType" : RevolveType.FULL, "oppositeDirection" : true});
        }
        {
            var Q0;
            Q0=makeQuery(id+"F17.imprint","IMPRINT",FACE,{"disambiguationData":[TD([[makeQuery(id+"F17.imprint","IMPRINT",EDGE,{"derivedFrom":sQuery(id+"F17.wireOp",EDGE,"E82.3.0")}),-1.0]])]});
            var Q1;
            Q1=sQuery(id+"F17.wireOp",EDGE,"E82.3.3");
            revolve(context, id + "F26", {"operationType" : NewBodyOperationType.REMOVE, "surfaceOperationType" : NewSurfaceOperationType.NEW, "entities" : qUnion([Q0]), "axis" : qUnion([Q1]), "revolveType" : RevolveType.FULL, "oppositeDirection" : true});
        }
        {
            var Q0;
            Q0=makeQuery(id+"F17.imprint","IMPRINT",FACE,{"disambiguationData":[TD([[makeQuery(id+"F17.imprint","IMPRINT",EDGE,{"derivedFrom":sQuery(id+"F17.wireOp",EDGE,"E82.2.0")}),-1.0]])]});
            var Q1;
            Q1=sQuery(id+"F17.wireOp",EDGE,"E82.2.3");
            revolve(context, id + "F27", {"operationType" : NewBodyOperationType.REMOVE, "surfaceOperationType" : NewSurfaceOperationType.NEW, "entities" : qUnion([Q0]), "axis" : qUnion([Q1]), "revolveType" : RevolveType.FULL, "oppositeDirection" : true});
        }
        {
            var Q0;
            Q0=makeQuery(id+"F17.imprint","IMPRINT",FACE,{"disambiguationData":[TD([[makeQuery(id+"F17.imprint","IMPRINT",EDGE,{"derivedFrom":sQuery(id+"F17.wireOp",EDGE,"E82.1.0")}),-1.0]])]});
            var Q1;
            Q1=sQuery(id+"F17.wireOp",EDGE,"E82.1.3");
            revolve(context, id + "F28", {"operationType" : NewBodyOperationType.REMOVE, "surfaceOperationType" : NewSurfaceOperationType.NEW, "entities" : qUnion([Q0]), "axis" : qUnion([Q1]), "revolveType" : RevolveType.FULL, "oppositeDirection" : true});
        }
        {
            var Q0;
            {var subQ0=sQuery(id+"F17.wireOp",EDGE,"E81");Q0=makeQuery(id+"F17.imprint","IMPRINT",FACE,{"disambiguationData":[TD([[makeQuery(id+"F17.imprint","IMPRINT",EDGE,{"derivedFrom":subQ0}),-1.0]])]});}
            var Q1;
            {var subQ0=sQuery(id+"F17.wireOp",EDGE,"E79");Q1=makeQuery(id+"F17.imprint","IMPRINT",FACE,{"disambiguationData":[TD([[makeQuery(id+"F17.imprint","IMPRINT",EDGE,{"derivedFrom":subQ0}),-1.0]])]});}
            var Q2;
            {var subQ0=sQuery(id+"F17.wireOp",EDGE,"E78");var subQ1=makeQuery(id+"F16.opExtrude","CAP_EDGE",EDGE,{"disambiguationData":[OSD([sQuery(id+"F15.wireOp",EDGE,"E42")])],"isStart":false});var subQ2=makeQuery(id+"F17.imprint","INTERSECT",VERTEX,{"derivedFrom":[subQ1,subQ0]});Q2=makeQuery(id+"F17.imprint","IMPRINT",FACE,{"disambiguationData":[TD([[makeQuery(id+"F17.imprint","IMPRINT",EDGE,{"disambiguationData":[TD([[subQ2,-1.0]])],"derivedFrom":subQ0}),-1.0]])]});}
            var Q3;
            Q3=sQuery(id+"F17.wireOp",EDGE,"E78");
            revolve(context, id + "F29", {"operationType" : NewBodyOperationType.REMOVE, "surfaceOperationType" : NewSurfaceOperationType.NEW, "entities" : qUnion([Q0, Q1, Q2]), "axis" : qUnion([Q3]), "revolveType" : RevolveType.FULL, "oppositeDirection" : true});
        }
    });
